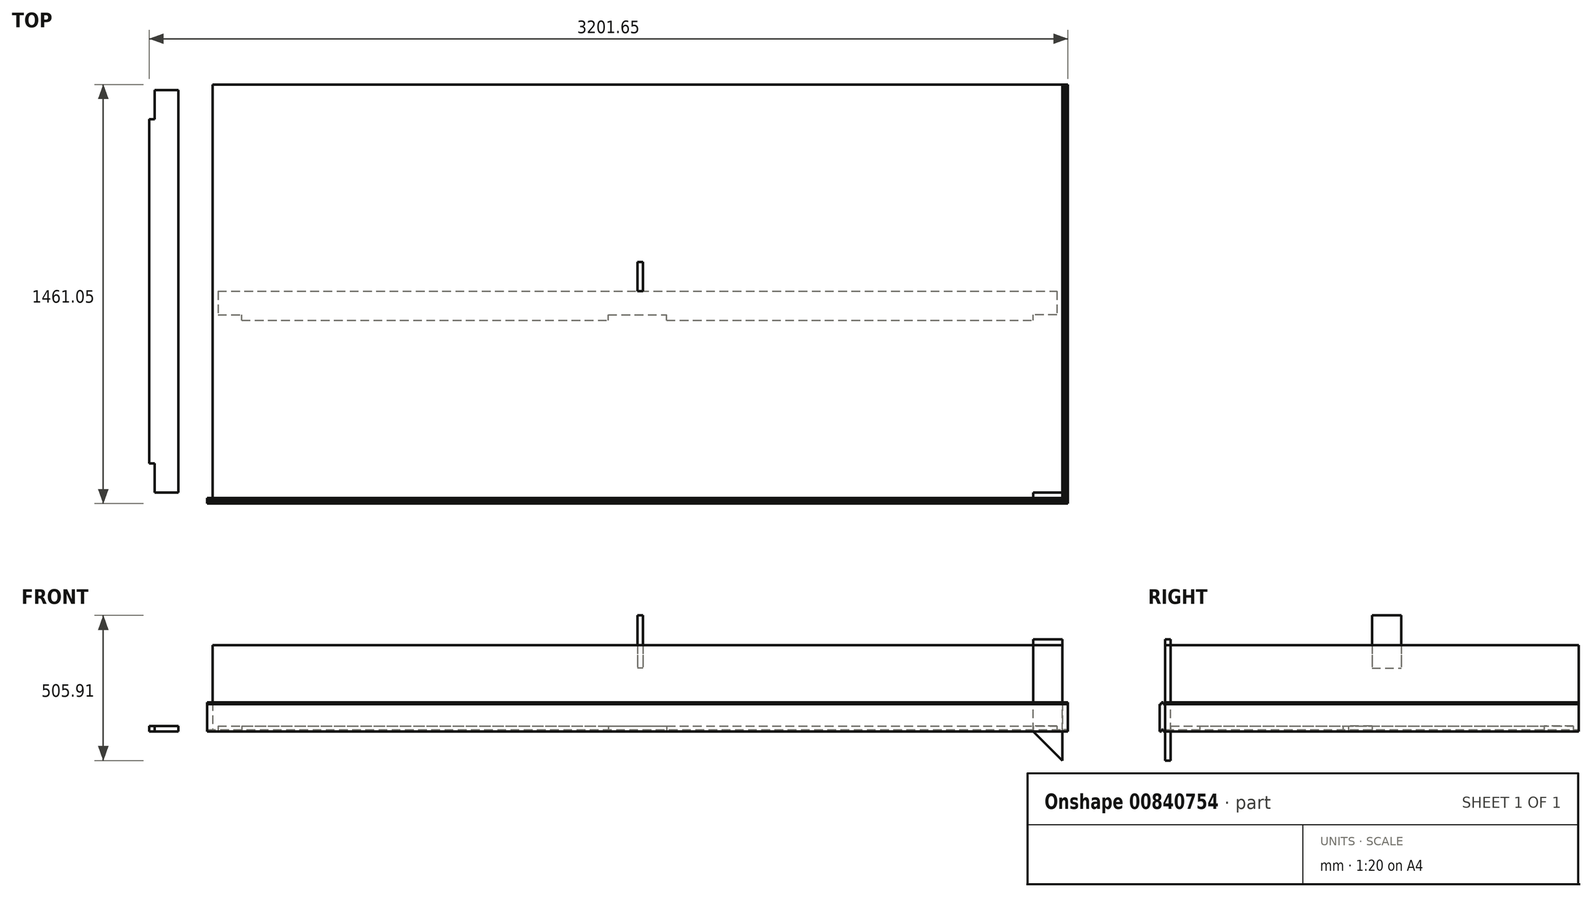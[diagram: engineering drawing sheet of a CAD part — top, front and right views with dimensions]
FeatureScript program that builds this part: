
annotation { "Feature Type Name" : "Feature", "Feature Type Description" : "" }
export const myFeature = defineFeature(function(context is Context, id is Id, definition is map)
    precondition{}
    {
        {
            var Q0;
            Q0=qCreatedBy(makeId("Right.planeOp"),FACE);
            cPlane(context, id + "F0", {"entities" : qUnion([Q0]), "cplaneType" : CPlaneType.OFFSET, "offset" : 1481 * mm, "width" : 150 * mm, "height" : 150 * mm});
        }
        {
            var Q0;
            Q0=qCreatedBy(makeId("Front.planeOp"),FACE);
            cPlane(context, id + "F1", {"entities" : qUnion([Q0]), "cplaneType" : CPlaneType.OFFSET, "offset" : 721 * mm, "width" : 150 * mm, "height" : 150 * mm});
        }
        {
            var Q0;
            Q0=qCreatedBy(makeId("Top.planeOp"),FACE);
            var sketch = newSketch(context, id + "F2", { "sketchPlane" : qUnion([Q0])});
            skLineSegment(sketch, "E0.bottom", {"start": v(1481, 721) * mm, "end": v(-1481, 721) * mm});
            skLineSegment(sketch, "E0.top", {"start": v(1481, -721) * mm, "end": v(-1481, -721) * mm});
            skLineSegment(sketch, "E0.left", {"start": v(1481, 721) * mm, "end": v(1481, -721) * mm});
            skLineSegment(sketch, "E0.right", {"start": v(-1481, 721) * mm, "end": v(-1481, -721) * mm});
            skPoint(sketch, "E0.middle", {"position": v(0, 0) * mm});
            skSolve(sketch);
        }
        {
            var Q0;
            Q0=qSketchRegion(id+"F2",true);
            extrude(context, id + "F3", {"entities" : qUnion([Q0]), "depth" : 300 * mm});
        }
        {
            var Q0;
            Q0=qCreatedBy(id+"F0.planeOp",FACE);
            var sketch = newSketch(context, id + "F4", { "sketchPlane" : qUnion([Q0])});
            skLineSegment(sketch, "E1.bottom", {"start": v(-721, 0) * mm, "end": v(721, 0) * mm});
            skLineSegment(sketch, "E1.top", {"start": v(-721, 101.6) * mm, "end": v(721, 101.6) * mm});
            skLineSegment(sketch, "E1.left", {"start": v(-721, 0) * mm, "end": v(-721, 101.6) * mm});
            skLineSegment(sketch, "E1.right", {"start": v(721, 0) * mm, "end": v(721, 101.6) * mm});
            skPoint(sketch, "E2", {"position": v(0, 0) * mm});
            skSolve(sketch);
        }
        {
            var Q0;
            Q0=qSketchRegion(id+"F4",true);
            extrude(context, id + "F5", {"entities" : qUnion([Q0]), "offsetDistance" : 25 * mm, "depth" : 19.05 * mm});
        }
        {
            var Q0;
            Q0=qCreatedBy(id+"F1.planeOp",FACE);
            var sketch = newSketch(context, id + "F6", { "sketchPlane" : qUnion([Q0])});
            skLineSegment(sketch, "E3.bottom", {"start": v(-1500, 101.6) * mm, "end": v(1500, 101.6) * mm});
            skLineSegment(sketch, "E3.top", {"start": v(-1500, 0) * mm, "end": v(1500, 0) * mm});
            skLineSegment(sketch, "E3.left", {"start": v(-1500, 101.6) * mm, "end": v(-1500, 0) * mm});
            skLineSegment(sketch, "E3.right", {"start": v(1500, 101.6) * mm, "end": v(1500, 0) * mm});
            skPoint(sketch, "E4", {"position": v(0, 0) * mm});
            skSolve(sketch);
        }
        {
            var Q0;
            Q0=qSketchRegion(id+"F6",true);
            extrude(context, id + "F7", {"entities" : qUnion([Q0]), "offsetDistance" : 25 * mm, "depth" : 19.05 * mm});
        }
        {
            var Q0;
            Q0=makeQuery(id+"F3.opExtrude","CAP_FACE",FACE,{"disambiguationData":[OSD([sQuery(id+"F2.wireOp",EDGE,"E0.bottom"),sQuery(id+"F2.wireOp",EDGE,"E0.top"),sQuery(id+"F2.wireOp",EDGE,"E0.left"),sQuery(id+"F2.wireOp",EDGE,"E0.right")])],"isStart":false});
            var sketch = newSketch(context, id + "F8", { "sketchPlane" : qUnion([Q0])});
            skFitSpline(sketch, "E5", {"points": [v(-9.76, -247.93) * mm, v(-14.36, -247) * mm, v(-98.7, -232.48) * mm, v(-197.18, -215.67) * mm]});
            skFitSpline(sketch, "E6", {"points": [v(-197.18, -215.67) * mm, v(-303.5, -197.52) * mm, v(-377.79, -184.02) * mm, v(-380.05, -182.43) * mm]});
            skFitSpline(sketch, "E7", {"points": [v(-380.05, -182.43) * mm, v(-386.35, -178.01) * mm, v(-389.22, -172.54) * mm, v(-390.38, -162.7) * mm]});
            skLineSegment(sketch, "E8", {"start": v(-390.38, -162.7) * mm, "end": v(-391.49, -153.38) * mm});
            skLineSegment(sketch, "E9", {"start": v(-391.49, -153.38) * mm, "end": v(-463.29, -153.35) * mm});
            skFitSpline(sketch, "E10", {"points": [v(-463.29, -153.35) * mm, v(-540.74, -153.32) * mm, v(-542.21, -153.15) * mm, v(-546.84, -143.5) * mm]});
            skFitSpline(sketch, "E11", {"points": [v(-546.84, -143.5) * mm, v(-550.32, -136.23) * mm, v(-547.5, -129.03) * mm, v(-539.62, -125.02) * mm]});
            skFitSpline(sketch, "E12", {"points": [v(-539.62, -125.02) * mm, v(-533.58, -121.95) * mm, v(-503.94, -121.77) * mm, v(0.65, -121.77) * mm]});
            skFitSpline(sketch, "E13", {"points": [v(0.65, -121.77) * mm, v(385.66, -121.76) * mm, v(536.18, -122.34) * mm, v(540.43, -123.82) * mm]});
            skFitSpline(sketch, "E14", {"points": [v(540.43, -123.82) * mm, v(543.67, -124.95) * mm, v(547.14, -127.4) * mm, v(548.14, -129.27) * mm]});
            skFitSpline(sketch, "E15", {"points": [v(548.14, -129.27) * mm, v(551.05, -134.7) * mm, v(550.26, -143.3) * mm, v(546.41, -148.06) * mm]});
            skLineSegment(sketch, "E16", {"start": v(546.41, -148.06) * mm, "end": v(542.86, -152.45) * mm});
            skLineSegment(sketch, "E17", {"start": v(542.86, -152.45) * mm, "end": v(467.85, -153.38) * mm});
            skLineSegment(sketch, "E18", {"start": v(467.85, -153.38) * mm, "end": v(392.83, -154.3) * mm});
            skLineSegment(sketch, "E19", {"start": v(392.83, -154.3) * mm, "end": v(392.5, -162.05) * mm});
            skFitSpline(sketch, "E20", {"points": [v(392.5, -162.05) * mm, v(391.99, -173.78) * mm, v(387.68, -180.46) * mm, v(378.46, -183.85) * mm]});
            skFitSpline(sketch, "E21", {"points": [v(378.46, -183.85) * mm, v(371.97, -186.24) * mm, v(2.57, -250.58) * mm, v(-0.47, -249.85) * mm]});
            skFitSpline(sketch, "E22", {"points": [v(-0.47, -249.85) * mm, v(-0.98, -249.73) * mm, v(-5.16, -248.87) * mm, v(-9.76, -247.93) * mm]});
            skLineSegment(sketch, "E23", {"start": v(-9.76, -247.93) * mm, "end": v(-9.76, -247.93) * mm});
            skFitSpline(sketch, "E24", {"points": [v(163.18, -91.34) * mm, v(144.56, -86.99) * mm, v(127.82, -80.58) * mm, v(118.25, -74.15) * mm]});
            skLineSegment(sketch, "E25", {"start": v(118.25, -74.15) * mm, "end": v(108.82, -67.8) * mm});
            skLineSegment(sketch, "E26", {"start": v(108.82, -67.8) * mm, "end": v(101.7, -74.22) * mm});
            skFitSpline(sketch, "E27", {"points": [v(101.7, -74.22) * mm, v(92.92, -82.15) * mm, v(86.06, -85.78) * mm, v(75.22, -88.2) * mm]});
            skFitSpline(sketch, "E28", {"points": [v(75.22, -88.2) * mm, v(52.86, -93.22) * mm, v(44.33, -75.76) * mm, v(50.52, -37.64) * mm]});
            skFitSpline(sketch, "E29", {"points": [v(50.52, -37.64) * mm, v(54.63, -12.34) * mm, v(54.44, -8.7) * mm, v(48.9, -6.17) * mm]});
            skFitSpline(sketch, "E30", {"points": [v(48.9, -6.17) * mm, v(42.7, -3.35) * mm, v(36.64, -7.44) * mm, v(29.87, -18.99) * mm]});
            skFitSpline(sketch, "E31", {"points": [v(29.87, -18.99) * mm, v(21.01, -34.1) * mm, v(18.43, -44.15) * mm, v(20.53, -55.3) * mm]});
            skFitSpline(sketch, "E32", {"points": [v(20.53, -55.3) * mm, v(21.54, -60.66) * mm, v(22.46, -68.35) * mm, v(22.57, -72.38) * mm]});
            skFitSpline(sketch, "E33", {"points": [v(22.57, -72.38) * mm, v(22.76, -78.97) * mm, v(22, -80.26) * mm, v(14.95, -85.23) * mm]});
            skFitSpline(sketch, "E34", {"points": [v(14.95, -85.23) * mm, v(4.39, -92.68) * mm, v(-7.54, -93.24) * mm, v(-11.04, -86.43) * mm]});
            skFitSpline(sketch, "E35", {"points": [v(-11.04, -86.43) * mm, v(-13.95, -80.76) * mm, v(-14.16, -56.28) * mm, v(-11.54, -26.93) * mm]});
            skFitSpline(sketch, "E36", {"points": [v(-11.54, -26.93) * mm, v(-9.2, -0.66) * mm, v(-9.84, 2.83) * mm, v(-17.07, 2.83) * mm]});
            skFitSpline(sketch, "E37", {"points": [v(-17.07, 2.83) * mm, v(-23.9, 2.83) * mm, v(-30.46, -4.7) * mm, v(-38.87, -22.23) * mm]});
            skFitSpline(sketch, "E38", {"points": [v(-38.87, -22.23) * mm, v(-45.93, -36.93) * mm, v(-46.62, -45.33) * mm, v(-42.27, -63.77) * mm]});
            skFitSpline(sketch, "E39", {"points": [v(-42.27, -63.77) * mm, v(-38.91, -78.01) * mm, v(-39.9, -80.3) * mm, v(-52.19, -87) * mm]});
            skFitSpline(sketch, "E40", {"points": [v(-52.19, -87) * mm, v(-68.26, -95.75) * mm, v(-75.2, -92.86) * mm, v(-77.56, -76.43) * mm]});
            skLineSegment(sketch, "E41", {"start": v(-77.56, -76.43) * mm, "end": v(-78.86, -67.36) * mm});
            skLineSegment(sketch, "E42", {"start": v(-78.86, -67.36) * mm, "end": v(-86.62, -74.83) * mm});
            skFitSpline(sketch, "E43", {"points": [v(-86.62, -74.83) * mm, v(-97.05, -84.9) * mm, v(-104.92, -88.54) * mm, v(-116.78, -88.82) * mm]});
            skFitSpline(sketch, "E44", {"points": [v(-116.78, -88.82) * mm, v(-128.34, -89.1) * mm, v(-132.94, -86) * mm, v(-138.3, -74.35) * mm]});
            skFitSpline(sketch, "E45", {"points": [v(-138.3, -74.35) * mm, v(-144.12, -61.65) * mm, v(-141.58, -31.54) * mm, v(-133.32, -15.58) * mm]});
            skLineSegment(sketch, "E46", {"start": v(-133.32, -15.58) * mm, "end": v(-130.44, -10) * mm});
            skLineSegment(sketch, "E47", {"start": v(-130.44, -10) * mm, "end": v(-141.2, -10.56) * mm});
            skLineSegment(sketch, "E48", {"start": v(-141.2, -10.56) * mm, "end": v(-151.94, -11.12) * mm});
            skLineSegment(sketch, "E49", {"start": v(-151.94, -11.12) * mm, "end": v(-155.34, -25.07) * mm});
            skFitSpline(sketch, "E50", {"points": [v(-155.34, -25.07) * mm, v(-157.97, -35.9) * mm, v(-158.52, -43.56) * mm, v(-157.8, -59.34) * mm]});
            skFitSpline(sketch, "E51", {"points": [v(-157.8, -59.34) * mm, v(-157.29, -70.85) * mm, v(-157.67, -81.12) * mm, v(-158.7, -83.03) * mm]});
            skFitSpline(sketch, "E52", {"points": [v(-158.7, -83.03) * mm, v(-161.25, -87.81) * mm, v(-170.24, -92.01) * mm, v(-177.92, -92.01) * mm]});
            skFitSpline(sketch, "E53", {"points": [v(-177.92, -92.01) * mm, v(-186.08, -92.01) * mm, v(-189.42, -87.45) * mm, v(-191.2, -73.87) * mm]});
            skLineSegment(sketch, "E54", {"start": v(-191.2, -73.87) * mm, "end": v(-192.48, -64.09) * mm});
            skLineSegment(sketch, "E55", {"start": v(-192.48, -64.09) * mm, "end": v(-200.42, -71.4) * mm});
            skFitSpline(sketch, "E56", {"points": [v(-200.42, -71.4) * mm, v(-209.89, -80.13) * mm, v(-220.17, -85.65) * mm, v(-231.87, -88.27) * mm]});
            skFitSpline(sketch, "E57", {"points": [v(-231.87, -88.27) * mm, v(-243.7, -90.92) * mm, v(-250.08, -87.49) * mm, v(-254.4, -76.16) * mm]});
            skLineSegment(sketch, "E58", {"start": v(-254.4, -76.16) * mm, "end": v(-257.65, -67.68) * mm});
            skLineSegment(sketch, "E59", {"start": v(-257.65, -67.68) * mm, "end": v(-262.94, -74.1) * mm});
            skFitSpline(sketch, "E60", {"points": [v(-262.94, -74.1) * mm, v(-279.38, -94.04) * mm, v(-316.37, -95.84) * mm, v(-331.85, -77.45) * mm]});
            skFitSpline(sketch, "E61", {"points": [v(-331.85, -77.45) * mm, v(-339.17, -68.75) * mm, v(-341.42, -59.86) * mm, v(-340.14, -44.75) * mm]});
            skFitSpline(sketch, "E62", {"points": [v(-340.14, -44.75) * mm, v(-338.13, -20.94) * mm, v(-329.14, -1.86) * mm, v(-313.1, 12.61) * mm]});
            skFitSpline(sketch, "E63", {"points": [v(-313.1, 12.61) * mm, v(-297.94, 26.32) * mm, v(-276.95, 32.69) * mm, v(-259.7, 28.82) * mm]});
            skFitSpline(sketch, "E64", {"points": [v(-259.7, 28.82) * mm, v(-252.55, 27.22) * mm, v(-250.45, 27.38) * mm, v(-247.85, 29.73) * mm]});
            skFitSpline(sketch, "E65", {"points": [v(-247.85, 29.73) * mm, v(-240.93, 36) * mm, v(-226.99, 30.32) * mm, v(-220.73, 18.7) * mm]});
            skLineSegment(sketch, "E66", {"start": v(-220.73, 18.7) * mm, "end": v(-217.21, 12.17) * mm});
            skLineSegment(sketch, "E67", {"start": v(-217.21, 12.17) * mm, "end": v(-223.2, 0.02) * mm});
            skFitSpline(sketch, "E68", {"points": [v(-223.2, 0.02) * mm, v(-228.92, -11.58) * mm, v(-229.19, -13.1) * mm, v(-229.16, -33.94) * mm]});
            skFitSpline(sketch, "E69", {"points": [v(-229.16, -33.94) * mm, v(-229.13, -57.9) * mm, v(-228.1, -61.48) * mm, v(-221.81, -59.49) * mm]});
            skFitSpline(sketch, "E70", {"points": [v(-221.81, -59.49) * mm, v(-215.07, -57.35) * mm, v(-188.28, -30.28) * mm, v(-188.28, -25.6) * mm]});
            skFitSpline(sketch, "E71", {"points": [v(-188.28, -25.6) * mm, v(-188.28, -23.36) * mm, v(-186.22, -15.85) * mm, v(-183.7, -8.92) * mm]});
            skFitSpline(sketch, "E72", {"points": [v(-183.7, -8.92) * mm, v(-179.26, 3.33) * mm, v(-179.23, 3.78) * mm, v(-182.54, 7.44) * mm]});
            skFitSpline(sketch, "E73", {"points": [v(-182.54, 7.44) * mm, v(-188.48, 13.98) * mm, v(-190.53, 19.67) * mm, v(-189.3, 26.21) * mm]});
            skFitSpline(sketch, "E74", {"points": [v(-189.3, 26.21) * mm, v(-187.82, 34.15) * mm, v(-182.12, 38.16) * mm, v(-172.31, 38.16) * mm]});
            skFitSpline(sketch, "E75", {"points": [v(-172.31, 38.16) * mm, v(-163.16, 38.16) * mm, v(-156.23, 32.34) * mm, v(-150.73, 20.03) * mm]});
            skFitSpline(sketch, "E76", {"points": [v(-150.73, 20.03) * mm, v(-147.7, 13.24) * mm, v(-146.4, 12.12) * mm, v(-141.55, 12.12) * mm]});
            skFitSpline(sketch, "E77", {"points": [v(-141.55, 12.12) * mm, v(-138.45, 12.12) * mm, v(-130.4, 14.33) * mm, v(-123.66, 17.03) * mm]});
            skFitSpline(sketch, "E78", {"points": [v(-123.66, 17.03) * mm, v(-109.3, 22.78) * mm, v(-107.41, 22.17) * mm, v(-101.2, 9.8) * mm]});
            skLineSegment(sketch, "E79", {"start": v(-101.2, 9.8) * mm, "end": v(-96.87, 1.18) * mm});
            skLineSegment(sketch, "E80", {"start": v(-96.87, 1.18) * mm, "end": v(-104.6, -26.95) * mm});
            skFitSpline(sketch, "E81", {"points": [v(-104.6, -26.95) * mm, v(-115.26, -65.72) * mm, v(-113.52, -68.38) * mm, v(-91.12, -47.46) * mm]});
            skLineSegment(sketch, "E82", {"start": v(-91.12, -47.46) * mm, "end": v(-77.26, -34.51) * mm});
            skLineSegment(sketch, "E83", {"start": v(-77.26, -34.51) * mm, "end": v(-76.15, -22.7) * mm});
            skFitSpline(sketch, "E84", {"points": [v(-76.15, -22.7) * mm, v(-74.76, -7.77) * mm, v(-68.68, 10.87) * mm, v(-61.04, 23.61) * mm]});
            skFitSpline(sketch, "E85", {"points": [v(-61.04, 23.61) * mm, v(-56.21, 31.68) * mm, v(-54.07, 33.61) * mm, v(-49.45, 34.07) * mm]});
            skFitSpline(sketch, "E86", {"points": [v(-49.45, 34.07) * mm, v(-44.95, 34.52) * mm, v(-42.63, 33.32) * mm, v(-38.15, 28.2) * mm]});
            skFitSpline(sketch, "E87", {"points": [v(-38.15, 28.2) * mm, v(-35.04, 24.67) * mm, v(-32.16, 20.74) * mm, v(-31.73, 19.46) * mm]});
            skFitSpline(sketch, "E88", {"points": [v(-31.73, 19.46) * mm, v(-31.21, 17.9) * mm, v(-28.37, 19.02) * mm, v(-23, 22.9) * mm]});
            skFitSpline(sketch, "E89", {"points": [v(-23, 22.9) * mm, v(-11.96, 30.9) * mm, v(-1.17, 32.3) * mm, v(9.54, 27.1) * mm]});
            skFitSpline(sketch, "E90", {"points": [v(9.54, 27.1) * mm, v(18.23, 22.9) * mm, v(22.7, 17.7) * mm, v(24.79, 9.4) * mm]});
            skLineSegment(sketch, "E91", {"start": v(24.79, 9.4) * mm, "end": v(26.04, 4.44) * mm});
            skLineSegment(sketch, "E92", {"start": v(26.04, 4.44) * mm, "end": v(30.92, 9.1) * mm});
            skFitSpline(sketch, "E93", {"points": [v(30.92, 9.1) * mm, v(43.6, 21.22) * mm, v(66.06, 25.1) * mm, v(77.8, 17.18) * mm]});
            skFitSpline(sketch, "E94", {"points": [v(77.8, 17.18) * mm, v(81.26, 14.85) * mm, v(85.14, 10.88) * mm, v(86.42, 8.35) * mm]});
            skFitSpline(sketch, "E95", {"points": [v(86.42, 8.35) * mm, v(90.04, 1.18) * mm, v(89.21, -14.95) * mm, v(84.14, -35.88) * mm]});
            skFitSpline(sketch, "E96", {"points": [v(84.14, -35.88) * mm, v(81.59, -46.43) * mm, v(79.5, -56.26) * mm, v(79.5, -57.73) * mm]});
            skFitSpline(sketch, "E97", {"points": [v(79.5, -57.73) * mm, v(79.5, -63.6) * mm, v(86.26, -59.69) * mm, v(100.97, -45.33) * mm]});
            skFitSpline(sketch, "E98", {"points": [v(100.97, -45.33) * mm, v(110.63, -35.9) * mm, v(117.25, -30.77) * mm, v(118.65, -31.64) * mm]});
            skFitSpline(sketch, "E99", {"points": [v(118.65, -31.64) * mm, v(120.17, -32.58) * mm, v(120.56, -36.5) * mm, v(119.89, -43.92) * mm]});
            skFitSpline(sketch, "E100", {"points": [v(119.89, -43.92) * mm, v(118.95, -54.29) * mm, v(119.1, -54.82) * mm, v(123.1, -54.82) * mm]});
            skFitSpline(sketch, "E101", {"points": [v(123.1, -54.82) * mm, v(127.02, -54.82) * mm, v(127.36, -53.84) * mm, v(128.4, -39.48) * mm]});
            skFitSpline(sketch, "E102", {"points": [v(128.4, -39.48) * mm, v(130.72, -7.09) * mm, v(148.03, 43.77) * mm, v(160.6, 55.09) * mm]});
            skFitSpline(sketch, "E103", {"points": [v(160.6, 55.09) * mm, v(178.01, 70.78) * mm, v(179.9, 58.14) * mm, v(168.42, 2.83) * mm]});
            skFitSpline(sketch, "E104", {"points": [v(168.42, 2.83) * mm, v(163.73, -19.8) * mm, v(158.67, -63.5) * mm, v(160.5, -65.68) * mm]});
            skFitSpline(sketch, "E105", {"points": [v(160.5, -65.68) * mm, v(161.76, -67.18) * mm, v(175.96, -69.61) * mm, v(183.63, -69.64) * mm]});
            skFitSpline(sketch, "E106", {"points": [v(183.63, -69.64) * mm, v(200.98, -69.71) * mm, v(215.69, -61.64) * mm, v(220.83, -49.22) * mm]});
            skFitSpline(sketch, "E107", {"points": [v(220.83, -49.22) * mm, v(224.51, -40.34) * mm, v(222.43, -16.02) * mm, v(217.28, -7.68) * mm]});
            skFitSpline(sketch, "E108", {"points": [v(217.28, -7.68) * mm, v(213.13, -0.96) * mm, v(212.95, -0.9) * mm, v(200.63, -0.9) * mm]});
            skFitSpline(sketch, "E109", {"points": [v(200.63, -0.9) * mm, v(187.27, -0.9) * mm, v(181.1, 1.8) * mm, v(179.39, 8.35) * mm]});
            skFitSpline(sketch, "E110", {"points": [v(179.39, 8.35) * mm, v(178.82, 10.5) * mm, v(179.82, 13.89) * mm, v(181.7, 16.2) * mm]});
            skFitSpline(sketch, "E111", {"points": [v(181.7, 16.2) * mm, v(184.4, 19.56) * mm, v(187.56, 20.46) * mm, v(199.63, 21.31) * mm]});
            skFitSpline(sketch, "E112", {"points": [v(199.63, 21.31) * mm, v(213.63, 22.3) * mm, v(214.4, 22.6) * mm, v(217.02, 27.93) * mm]});
            skFitSpline(sketch, "E113", {"points": [v(217.02, 27.93) * mm, v(218.53, 31) * mm, v(219.77, 38.53) * mm, v(219.78, 44.67) * mm]});
            skFitSpline(sketch, "E114", {"points": [v(219.78, 44.67) * mm, v(219.8, 64.17) * mm, v(211.17, 71.67) * mm, v(187.07, 73.1) * mm]});
            skFitSpline(sketch, "E115", {"points": [v(187.07, 73.1) * mm, v(170.05, 74.11) * mm, v(157.7, 71.45) * mm, v(139.99, 62.97) * mm]});
            skFitSpline(sketch, "E116", {"points": [v(139.99, 62.97) * mm, v(124.82, 55.7) * mm, v(118.55, 54.98) * mm, v(118.55, 60.51) * mm]});
            skFitSpline(sketch, "E117", {"points": [v(118.55, 60.51) * mm, v(118.55, 70.5) * mm, v(143.11, 88.38) * mm, v(165.9, 94.95) * mm]});
            skFitSpline(sketch, "E118", {"points": [v(165.9, 94.95) * mm, v(181.16, 99.36) * mm, v(211.58, 97.92) * mm, v(227.33, 92.04) * mm]});
            skFitSpline(sketch, "E119", {"points": [v(227.33, 92.04) * mm, v(241.91, 86.6) * mm, v(254.67, 73.92) * mm, v(257.71, 61.83) * mm]});
            skFitSpline(sketch, "E120", {"points": [v(257.71, 61.83) * mm, v(262.48, 42.9) * mm, v(259.33, 31.38) * mm, v(245.79, 18.17) * mm]});
            skFitSpline(sketch, "E121", {"points": [v(245.79, 18.17) * mm, v(240.28, 12.8) * mm, v(236.48, 8.4) * mm, v(237.34, 8.4) * mm]});
            skFitSpline(sketch, "E122", {"points": [v(237.34, 8.4) * mm, v(241.01, 8.4) * mm, v(256.17, -7.19) * mm, v(259.81, -14.71) * mm]});
            skFitSpline(sketch, "E123", {"points": [v(259.81, -14.71) * mm, v(265.46, -26.39) * mm, v(265.68, -49.04) * mm, v(260.25, -59.68) * mm]});
            skFitSpline(sketch, "E124", {"points": [v(260.25, -59.68) * mm, v(254.38, -71.16) * mm, v(239.5, -83.55) * mm, v(225.92, -88.28) * mm]});
            skFitSpline(sketch, "E125", {"points": [v(225.92, -88.28) * mm, v(211.44, -93.33) * mm, v(178.53, -94.93) * mm, v(163.18, -91.34) * mm]});
            skFitSpline(sketch, "E126", {"points": [v(-281.84, -62.14) * mm, v(-267.85, -56.85) * mm, v(-259.05, -41.8) * mm, v(-258.98, -23.08) * mm]});
            skFitSpline(sketch, "E127", {"points": [v(-258.98, -23.08) * mm, v(-258.96, -16.37) * mm, v(-258.05, -6.04) * mm, v(-256.95, -0.12) * mm]});
            skFitSpline(sketch, "E128", {"points": [v(-256.95, -0.12) * mm, v(-255.86, 5.8) * mm, v(-255.42, 11.09) * mm, v(-255.98, 11.64) * mm]});
            skFitSpline(sketch, "E129", {"points": [v(-255.98, 11.64) * mm, v(-257.93, 13.6) * mm, v(-273.99, 6.15) * mm, v(-282.7, -0.75) * mm]});
            skFitSpline(sketch, "E130", {"points": [v(-282.7, -0.75) * mm, v(-295.24, -10.66) * mm, v(-302.1, -24.16) * mm, v(-303.18, -41.06) * mm]});
            skFitSpline(sketch, "E131", {"points": [v(-303.18, -41.06) * mm, v(-303.98, -53.62) * mm, v(-303.72, -54.84) * mm, v(-299.24, -59.32) * mm]});
            skFitSpline(sketch, "E132", {"points": [v(-299.24, -59.32) * mm, v(-294.03, -64.53) * mm, v(-289.93, -65.2) * mm, v(-281.84, -62.14) * mm]});
            skFitSpline(sketch, "E133", {"points": [v(-459.3, -89.94) * mm, v(-464.48, -84.62) * mm, v(-460.7, -35.47) * mm, v(-453.32, -12.23) * mm]});
            skFitSpline(sketch, "E134", {"points": [v(-453.32, -12.23) * mm, v(-452.15, -8.52) * mm, v(-452.73, -8.33) * mm, v(-465.23, -8.33) * mm]});
            skFitSpline(sketch, "E135", {"points": [v(-465.23, -8.33) * mm, v(-476.68, -8.33) * mm, v(-478.37, -7.9) * mm, v(-478.37, -4.96) * mm]});
            skFitSpline(sketch, "E136", {"points": [v(-478.37, -4.96) * mm, v(-478.37, 0.26) * mm, v(-468.99, 8.03) * mm, v(-457.1, 12.63) * mm]});
            skLineSegment(sketch, "E137", {"start": v(-457.1, 12.63) * mm, "end": v(-446.32, 16.8) * mm});
            skLineSegment(sketch, "E138", {"start": v(-446.32, 16.8) * mm, "end": v(-438.43, 39.1) * mm});
            skFitSpline(sketch, "E139", {"points": [v(-438.43, 39.1) * mm, v(-434.08, 51.37) * mm, v(-429.87, 62.96) * mm, v(-429.07, 64.87) * mm]});
            skFitSpline(sketch, "E140", {"points": [v(-429.07, 64.87) * mm, v(-427.72, 68.05) * mm, v(-428.28, 68.22) * mm, v(-435.78, 67) * mm]});
            skFitSpline(sketch, "E141", {"points": [v(-435.78, 67) * mm, v(-447.95, 65.04) * mm, v(-458.5, 59.86) * mm, v(-467.75, 51.34) * mm]});
            skFitSpline(sketch, "E142", {"points": [v(-467.75, 51.34) * mm, v(-479.66, 40.36) * mm, v(-483.95, 41.51) * mm, v(-483.95, 55.7) * mm]});
            skFitSpline(sketch, "E143", {"points": [v(-483.95, 55.7) * mm, v(-483.95, 68.83) * mm, v(-467.73, 83.32) * mm, v(-445.28, 90.26) * mm]});
            skFitSpline(sketch, "E144", {"points": [v(-445.28, 90.26) * mm, v(-427.1, 95.87) * mm, v(-406.05, 97.33) * mm, v(-358.74, 96.25) * mm]});
            skFitSpline(sketch, "E145", {"points": [v(-358.74, 96.25) * mm, v(-311.18, 95.17) * mm, v(-311.95, 95.43) * mm, v(-317.58, 82.22) * mm]});
            skFitSpline(sketch, "E146", {"points": [v(-317.58, 82.22) * mm, v(-323.64, 68.03) * mm, v(-324, 67.91) * mm, v(-360.96, 67.88) * mm]});
            skLineSegment(sketch, "E147", {"start": v(-360.96, 67.88) * mm, "end": v(-393.76, 67.85) * mm});
            skLineSegment(sketch, "E148", {"start": v(-393.76, 67.85) * mm, "end": v(-398.66, 47.9) * mm});
            skFitSpline(sketch, "E149", {"points": [v(-398.66, 47.9) * mm, v(-401.36, 36.91) * mm, v(-403.87, 26.67) * mm, v(-404.24, 25.14) * mm]});
            skFitSpline(sketch, "E150", {"points": [v(-404.24, 25.14) * mm, v(-404.8, 22.8) * mm, v(-401.23, 22.27) * mm, v(-381.74, 21.83) * mm]});
            skFitSpline(sketch, "E151", {"points": [v(-381.74, 21.83) * mm, v(-367.15, 21.5) * mm, v(-358.1, 20.53) * mm, v(-357.28, 19.21) * mm]});
            skFitSpline(sketch, "E152", {"points": [v(-357.28, 19.21) * mm, v(-355.76, 16.75) * mm, v(-359.89, 2.02) * mm, v(-363.24, -2.01) * mm]});
            skFitSpline(sketch, "E153", {"points": [v(-363.24, -2.01) * mm, v(-365.2, -4.38) * mm, v(-369.3, -4.62) * mm, v(-389.06, -3.54) * mm]});
            skLineSegment(sketch, "E154", {"start": v(-389.06, -3.54) * mm, "end": v(-412.56, -2.27) * mm});
            skLineSegment(sketch, "E155", {"start": v(-412.56, -2.27) * mm, "end": v(-416.52, -18.78) * mm});
            skFitSpline(sketch, "E156", {"points": [v(-416.52, -18.78) * mm, v(-421.04, -37.64) * mm, v(-423.77, -53.93) * mm, v(-425.45, -72.08) * mm]});
            skFitSpline(sketch, "E157", {"points": [v(-425.45, -72.08) * mm, v(-426.44, -82.86) * mm, v(-427.3, -85.14) * mm, v(-431.33, -87.78) * mm]});
            skFitSpline(sketch, "E158", {"points": [v(-431.33, -87.78) * mm, v(-437.41, -91.77) * mm, v(-456.13, -93.2) * mm, v(-459.3, -89.94) * mm]});
            skFitSpline(sketch, "E159", {"points": [v(317.5, -88.5) * mm, v(302.9, -83.79) * mm, v(289.51, -71.3) * mm, v(285.81, -58.96) * mm]});
            skFitSpline(sketch, "E160", {"points": [v(285.81, -58.96) * mm, v(282.17, -46.8) * mm, v(284.25, -22.14) * mm, v(289.96, -9.87) * mm]});
            skFitSpline(sketch, "E161", {"points": [v(289.96, -9.87) * mm, v(299.26, 10.12) * mm, v(316.09, 24.32) * mm, v(335.9, 28.9) * mm]});
            skFitSpline(sketch, "E162", {"points": [v(335.9, 28.9) * mm, v(354.07, 33.1) * mm, v(378.44, 28.13) * mm, v(386.33, 18.63) * mm]});
            skFitSpline(sketch, "E163", {"points": [v(386.33, 18.63) * mm, v(390.02, 14.18) * mm, v(386.8, 12.82) * mm, v(369.86, 11.65) * mm]});
            skFitSpline(sketch, "E164", {"points": [v(369.86, 11.65) * mm, v(362, 11.12) * mm, v(352.6, 9.43) * mm, v(348.96, 7.91) * mm]});
            skFitSpline(sketch, "E165", {"points": [v(348.96, 7.91) * mm, v(331.95, 0.8) * mm, v(320.77, -16.17) * mm, v(320.52, -35.3) * mm]});
            skFitSpline(sketch, "E166", {"points": [v(320.52, -35.3) * mm, v(320.22, -57.93) * mm, v(334.52, -68.41) * mm, v(357.15, -62.13) * mm]});
            skLineSegment(sketch, "E167", {"start": v(357.15, -62.13) * mm, "end": v(364.23, -60.16) * mm});
            skLineSegment(sketch, "E168", {"start": v(364.23, -60.16) * mm, "end": v(357.84, -53.09) * mm});
            skFitSpline(sketch, "E169", {"points": [v(357.84, -53.09) * mm, v(336.45, -29.41) * mm, v(349.03, 6.55) * mm, v(378.7, 6.55) * mm]});
            skFitSpline(sketch, "E170", {"points": [v(378.7, 6.55) * mm, v(389.23, 6.55) * mm, v(395.06, 3.8) * mm, v(399.43, -3.17) * mm]});
            skFitSpline(sketch, "E171", {"points": [v(399.43, -3.17) * mm, v(402.65, -8.3) * mm, v(403.12, -11.47) * mm, v(402.44, -23.2) * mm]});
            skFitSpline(sketch, "E172", {"points": [v(402.44, -23.2) * mm, v(402, -30.88) * mm, v(401.02, -39.04) * mm, v(400.27, -41.34) * mm]});
            skFitSpline(sketch, "E173", {"points": [v(400.27, -41.34) * mm, v(398.58, -46.51) * mm, v(402.33, -46.92) * mm, v(411.06, -42.52) * mm]});
            skFitSpline(sketch, "E174", {"points": [v(411.06, -42.52) * mm, v(421.31, -37.33) * mm, v(425.37, -32.45) * mm, v(425.44, -25.2) * mm]});
            skFitSpline(sketch, "E175", {"points": [v(425.44, -25.2) * mm, v(425.48, -21.55) * mm, v(426.6, -12.92) * mm, v(427.94, -6.02) * mm]});
            skFitSpline(sketch, "E176", {"points": [v(427.94, -6.02) * mm, v(429.27, 0.87) * mm, v(429.94, 6.94) * mm, v(429.42, 7.46) * mm]});
            skFitSpline(sketch, "E177", {"points": [v(429.42, 7.46) * mm, v(428.9, 7.98) * mm, v(425.6, 8.4) * mm, v(422.07, 8.4) * mm]});
            skFitSpline(sketch, "E178", {"points": [v(422.07, 8.4) * mm, v(415.71, 8.4) * mm, v(415.67, 8.46) * mm, v(416.93, 15.14) * mm]});
            skFitSpline(sketch, "E179", {"points": [v(416.93, 15.14) * mm, v(418.93, 25.81) * mm, v(421.68, 28.86) * mm, v(429.3, 28.86) * mm]});
            skFitSpline(sketch, "E180", {"points": [v(429.3, 28.86) * mm, v(435.8, 28.86) * mm, v(436.17, 29.23) * mm, v(439.97, 39.55) * mm]});
            skFitSpline(sketch, "E181", {"points": [v(439.97, 39.55) * mm, v(450.84, 69.05) * mm, v(465.01, 75.94) * mm, v(473.83, 56) * mm]});
            skLineSegment(sketch, "E182", {"start": v(473.83, 56) * mm, "end": v(477.45, 47.84) * mm});
            skLineSegment(sketch, "E183", {"start": v(477.45, 47.84) * mm, "end": v(472.82, 39.75) * mm});
            skFitSpline(sketch, "E184", {"points": [v(472.82, 39.75) * mm, v(470.27, 35.3) * mm, v(468.18, 31.02) * mm, v(468.17, 30.25) * mm]});
            skFitSpline(sketch, "E185", {"points": [v(468.17, 30.25) * mm, v(468.15, 29.49) * mm, v(474, 28.86) * mm, v(481.16, 28.86) * mm]});
            skFitSpline(sketch, "E186", {"points": [v(481.16, 28.86) * mm, v(493.59, 28.86) * mm, v(494.18, 28.66) * mm, v(494.18, 24.49) * mm]});
            skFitSpline(sketch, "E187", {"points": [v(494.18, 24.49) * mm, v(494.18, 22.08) * mm, v(493.26, 17.48) * mm, v(492.14, 14.26) * mm]});
            skFitSpline(sketch, "E188", {"points": [v(492.14, 14.26) * mm, v(490.1, 8.41) * mm, v(490.07, 8.4) * mm, v(476.53, 8.4) * mm]});
            skFitSpline(sketch, "E189", {"points": [v(476.53, 8.4) * mm, v(466.58, 8.4) * mm, v(462.7, 7.7) * mm, v(461.96, 5.79) * mm]});
            skFitSpline(sketch, "E190", {"points": [v(461.96, 5.79) * mm, v(461.4, 4.35) * mm, v(459.93, -6.74) * mm, v(458.69, -18.85) * mm]});
            skFitSpline(sketch, "E191", {"points": [v(458.69, -18.85) * mm, v(456.19, -43.13) * mm, v(457.42, -58.1) * mm, v(462.05, -59.89) * mm]});
            skFitSpline(sketch, "E192", {"points": [v(462.05, -59.89) * mm, v(466.54, -61.6) * mm, v(480.7, -53.25) * mm, v(493.44, -41.34) * mm]});
            skFitSpline(sketch, "E193", {"points": [v(493.44, -41.34) * mm, v(499.73, -35.46) * mm, v(505.73, -30.65) * mm, v(506.77, -30.65) * mm]});
            skFitSpline(sketch, "E194", {"points": [v(506.77, -30.65) * mm, v(510.1, -30.65) * mm, v(511.02, -39.58) * mm, v(508.46, -47.01) * mm]});
            skFitSpline(sketch, "E195", {"points": [v(508.46, -47.01) * mm, v(500.27, -70.78) * mm, v(464.23, -93.67) * mm, v(443.63, -88.18) * mm]});
            skFitSpline(sketch, "E196", {"points": [v(443.63, -88.18) * mm, v(436.32, -86.23) * mm, v(430.49, -78.96) * mm, v(428.05, -68.77) * mm]});
            skFitSpline(sketch, "E197", {"points": [v(428.05, -68.77) * mm, v(426, -60.18) * mm, v(425.55, -59.99) * mm, v(418.25, -64.52) * mm]});
            skFitSpline(sketch, "E198", {"points": [v(418.25, -64.52) * mm, v(412.67, -68) * mm, v(408.97, -68.73) * mm, v(397.88, -68.57) * mm]});
            skFitSpline(sketch, "E199", {"points": [v(397.88, -68.57) * mm, v(384.98, -68.4) * mm, v(384.01, -68.68) * mm, v(377.5, -74.64) * mm]});
            skFitSpline(sketch, "E200", {"points": [v(377.5, -74.64) * mm, v(365.8, -85.37) * mm, v(355.8, -89.15) * mm, v(337.98, -89.6) * mm]});
            skFitSpline(sketch, "E201", {"points": [v(337.98, -89.6) * mm, v(329.28, -89.82) * mm, v(320.07, -89.33) * mm, v(317.5, -88.5) * mm]});
            skFitSpline(sketch, "E202", {"points": [v(385.7, -25.43) * mm, v(386.64, -17.46) * mm, v(386.3, -15.64) * mm, v(383.66, -14.63) * mm]});
            skFitSpline(sketch, "E203", {"points": [v(383.66, -14.63) * mm, v(379.08, -12.87) * mm, v(376.38, -16.52) * mm, v(376.67, -24.09) * mm]});
            skFitSpline(sketch, "E204", {"points": [v(376.67, -24.09) * mm, v(376.97, -32.15) * mm, v(380.4, -39.18) * mm, v(382.83, -36.75) * mm]});
            skFitSpline(sketch, "E205", {"points": [v(382.83, -36.75) * mm, v(383.78, -35.8) * mm, v(385.07, -30.7) * mm, v(385.7, -25.43) * mm]});
            skFitSpline(sketch, "E206", {"points": [v(-539.73, 126.1) * mm, v(-551.06, 131.84) * mm, v(-551, 146.27) * mm, v(-539.62, 152.05) * mm]});
            skFitSpline(sketch, "E207", {"points": [v(-539.62, 152.05) * mm, v(-533.86, 154.98) * mm, v(-526.13, 155.3) * mm, v(-462.1, 155.3) * mm]});
            skLineSegment(sketch, "E208", {"start": v(-462.1, 155.3) * mm, "end": v(-390.97, 155.3) * mm});
            skLineSegment(sketch, "E209", {"start": v(-390.97, 155.3) * mm, "end": v(-390.97, 160.85) * mm});
            skFitSpline(sketch, "E210", {"points": [v(-390.97, 160.85) * mm, v(-390.97, 170.05) * mm, v(-385.48, 181.2) * mm, v(-379.4, 184.35) * mm]});
            skFitSpline(sketch, "E211", {"points": [v(-379.4, 184.35) * mm, v(-373.17, 187.57) * mm, v(-10.28, 250.15) * mm, v(2.18, 250.15) * mm]});
            skFitSpline(sketch, "E212", {"points": [v(2.18, 250.15) * mm, v(10.33, 250.15) * mm, v(362.94, 190.41) * mm, v(375.5, 186.9) * mm]});
            skFitSpline(sketch, "E213", {"points": [v(375.5, 186.9) * mm, v(384.93, 184.27) * mm, v(391.52, 175.86) * mm, v(393.02, 164.53) * mm]});
            skLineSegment(sketch, "E214", {"start": v(393.02, 164.53) * mm, "end": v(394.24, 155.3) * mm});
            skLineSegment(sketch, "E215", {"start": v(394.24, 155.3) * mm, "end": v(464.39, 155.3) * mm});
            skFitSpline(sketch, "E216", {"points": [v(464.39, 155.3) * mm, v(536.67, 155.3) * mm, v(544.5, 154.6) * mm, v(548.14, 147.8) * mm]});
            skFitSpline(sketch, "E217", {"points": [v(548.14, 147.8) * mm, v(551.05, 142.36) * mm, v(550.26, 133.77) * mm, v(546.41, 129.02) * mm]});
            skLineSegment(sketch, "E218", {"start": v(546.41, 129.02) * mm, "end": v(542.86, 124.63) * mm});
            skLineSegment(sketch, "E219", {"start": v(542.86, 124.63) * mm, "end": v(3.88, 124.18) * mm});
            skFitSpline(sketch, "E220", {"points": [v(3.88, 124.18) * mm, v(-428.24, 123.83) * mm, v(-536, 124.2) * mm, v(-539.73, 126.1) * mm]});
            skLineSegment(sketch, "E221", {"start": v(-539.73, 126.1) * mm, "end": v(-539.73, 126.1) * mm});
            skSolve(sketch);
        }
        {
            var Q0;
            Q0=makeQuery(id+"F5.opExtrude","CAP_FACE",FACE,{"disambiguationData":[OSD([sQuery(id+"F4.wireOp",EDGE,"E1.bottom"),sQuery(id+"F4.wireOp",EDGE,"E1.top"),sQuery(id+"F4.wireOp",EDGE,"E1.left"),sQuery(id+"F4.wireOp",EDGE,"E1.right")])],"isStart":false});
            var sketch = newSketch(context, id + "F9", { "sketchPlane" : qUnion([Q0])});
            skFitSpline(sketch, "E222", {"points": [v(-4.02, 72.8) * mm, v(-5.86, 73.18) * mm, v(-39.6, 78.99) * mm, v(-78.98, 85.71) * mm]});
            skFitSpline(sketch, "E223", {"points": [v(-78.98, 85.71) * mm, v(-121.51, 92.97) * mm, v(-151.23, 98.37) * mm, v(-152.13, 99) * mm]});
            skFitSpline(sketch, "E224", {"points": [v(-152.13, 99) * mm, v(-154.65, 100.77) * mm, v(-155.8, 102.96) * mm, v(-156.27, 106.9) * mm]});
            skLineSegment(sketch, "E225", {"start": v(-156.27, 106.9) * mm, "end": v(-156.7, 110.63) * mm});
            skLineSegment(sketch, "E226", {"start": v(-156.7, 110.63) * mm, "end": v(-185.43, 110.64) * mm});
            skFitSpline(sketch, "E227", {"points": [v(-185.43, 110.64) * mm, v(-216.4, 110.65) * mm, v(-217, 110.72) * mm, v(-218.85, 114.58) * mm]});
            skFitSpline(sketch, "E228", {"points": [v(-218.85, 114.58) * mm, v(-220.24, 117.49) * mm, v(-219.12, 120.37) * mm, v(-215.96, 121.97) * mm]});
            skFitSpline(sketch, "E229", {"points": [v(-215.96, 121.97) * mm, v(-213.54, 123.2) * mm, v(-201.69, 123.27) * mm, v(0.15, 123.27) * mm]});
            skFitSpline(sketch, "E230", {"points": [v(0.15, 123.27) * mm, v(154.15, 123.27) * mm, v(214.36, 123.04) * mm, v(216.06, 122.45) * mm]});
            skFitSpline(sketch, "E231", {"points": [v(216.06, 122.45) * mm, v(217.36, 122) * mm, v(218.75, 121.02) * mm, v(219.15, 120.27) * mm]});
            skFitSpline(sketch, "E232", {"points": [v(219.15, 120.27) * mm, v(220.3, 118.1) * mm, v(220, 114.66) * mm, v(218.45, 112.76) * mm]});
            skLineSegment(sketch, "E233", {"start": v(218.45, 112.76) * mm, "end": v(217.03, 111) * mm});
            skLineSegment(sketch, "E234", {"start": v(217.03, 111) * mm, "end": v(187.03, 110.63) * mm});
            skLineSegment(sketch, "E235", {"start": v(187.03, 110.63) * mm, "end": v(157.02, 110.26) * mm});
            skLineSegment(sketch, "E236", {"start": v(157.02, 110.26) * mm, "end": v(156.89, 107.16) * mm});
            skFitSpline(sketch, "E237", {"points": [v(156.89, 107.16) * mm, v(156.68, 102.47) * mm, v(154.96, 99.8) * mm, v(151.27, 98.44) * mm]});
            skFitSpline(sketch, "E238", {"points": [v(151.27, 98.44) * mm, v(148.68, 97.48) * mm, v(0.92, 71.75) * mm, v(-0.3, 72.04) * mm]});
            skFitSpline(sketch, "E239", {"points": [v(-0.3, 72.04) * mm, v(-0.5, 72.09) * mm, v(-2.18, 72.43) * mm, v(-4.02, 72.8) * mm]});
            skLineSegment(sketch, "E240", {"start": v(-4.02, 72.8) * mm, "end": v(-4.02, 72.8) * mm});
            skFitSpline(sketch, "E241", {"points": [v(65.16, 135.44) * mm, v(57.71, 137.18) * mm, v(51.02, 139.75) * mm, v(47.2, 142.32) * mm]});
            skLineSegment(sketch, "E242", {"start": v(47.2, 142.32) * mm, "end": v(43.41, 144.86) * mm});
            skLineSegment(sketch, "E243", {"start": v(43.41, 144.86) * mm, "end": v(40.57, 142.3) * mm});
            skFitSpline(sketch, "E244", {"points": [v(40.57, 142.3) * mm, v(37.06, 139.12) * mm, v(34.31, 137.67) * mm, v(29.98, 136.7) * mm]});
            skFitSpline(sketch, "E245", {"points": [v(29.98, 136.7) * mm, v(21.03, 134.7) * mm, v(17.62, 141.67) * mm, v(20.1, 156.92) * mm]});
            skFitSpline(sketch, "E246", {"points": [v(20.1, 156.92) * mm, v(21.74, 167.04) * mm, v(21.67, 168.5) * mm, v(19.44, 169.51) * mm]});
            skFitSpline(sketch, "E247", {"points": [v(19.44, 169.51) * mm, v(16.97, 170.64) * mm, v(14.54, 169) * mm, v(11.84, 164.39) * mm]});
            skFitSpline(sketch, "E248", {"points": [v(11.84, 164.39) * mm, v(8.3, 158.34) * mm, v(7.26, 154.32) * mm, v(8.1, 149.86) * mm]});
            skFitSpline(sketch, "E249", {"points": [v(8.1, 149.86) * mm, v(8.5, 147.71) * mm, v(8.87, 144.64) * mm, v(8.92, 143.03) * mm]});
            skFitSpline(sketch, "E250", {"points": [v(8.92, 143.03) * mm, v(9, 140.4) * mm, v(8.69, 139.88) * mm, v(5.87, 137.89) * mm]});
            skFitSpline(sketch, "E251", {"points": [v(5.87, 137.89) * mm, v(1.64, 134.9) * mm, v(-3.13, 134.68) * mm, v(-4.53, 137.4) * mm]});
            skFitSpline(sketch, "E252", {"points": [v(-4.53, 137.4) * mm, v(-5.7, 139.68) * mm, v(-5.78, 149.47) * mm, v(-4.73, 161.2) * mm]});
            skFitSpline(sketch, "E253", {"points": [v(-4.73, 161.2) * mm, v(-3.79, 171.71) * mm, v(-4.05, 173.1) * mm, v(-6.94, 173.1) * mm]});
            skFitSpline(sketch, "E254", {"points": [v(-6.94, 173.1) * mm, v(-9.67, 173.1) * mm, v(-12.3, 170.1) * mm, v(-15.66, 163.09) * mm]});
            skFitSpline(sketch, "E255", {"points": [v(-15.66, 163.09) * mm, v(-18.48, 157.2) * mm, v(-18.76, 153.85) * mm, v(-17.02, 146.47) * mm]});
            skFitSpline(sketch, "E256", {"points": [v(-17.02, 146.47) * mm, v(-15.68, 140.78) * mm, v(-16.07, 139.86) * mm, v(-20.99, 137.18) * mm]});
            skFitSpline(sketch, "E257", {"points": [v(-20.99, 137.18) * mm, v(-27.42, 133.68) * mm, v(-30.19, 134.83) * mm, v(-31.13, 141.4) * mm]});
            skLineSegment(sketch, "E258", {"start": v(-31.13, 141.4) * mm, "end": v(-31.66, 145.04) * mm});
            skLineSegment(sketch, "E259", {"start": v(-31.66, 145.04) * mm, "end": v(-34.76, 142.05) * mm});
            skFitSpline(sketch, "E260", {"points": [v(-34.76, 142.05) * mm, v(-38.93, 138.02) * mm, v(-42.08, 136.56) * mm, v(-46.82, 136.45) * mm]});
            skFitSpline(sketch, "E261", {"points": [v(-46.82, 136.45) * mm, v(-51.45, 136.34) * mm, v(-53.29, 137.58) * mm, v(-55.43, 142.24) * mm]});
            skFitSpline(sketch, "E262", {"points": [v(-55.43, 142.24) * mm, v(-57.76, 147.32) * mm, v(-56.74, 159.36) * mm, v(-53.44, 165.75) * mm]});
            skLineSegment(sketch, "E263", {"start": v(-53.44, 165.75) * mm, "end": v(-52.29, 167.98) * mm});
            skLineSegment(sketch, "E264", {"start": v(-52.29, 167.98) * mm, "end": v(-56.59, 167.76) * mm});
            skLineSegment(sketch, "E265", {"start": v(-56.59, 167.76) * mm, "end": v(-60.89, 167.53) * mm});
            skLineSegment(sketch, "E266", {"start": v(-60.89, 167.53) * mm, "end": v(-62.25, 161.95) * mm});
            skFitSpline(sketch, "E267", {"points": [v(-62.25, 161.95) * mm, v(-63.3, 157.62) * mm, v(-63.52, 154.56) * mm, v(-63.24, 148.25) * mm]});
            skFitSpline(sketch, "E268", {"points": [v(-63.24, 148.25) * mm, v(-63.03, 143.64) * mm, v(-63.18, 139.53) * mm, v(-63.59, 138.77) * mm]});
            skFitSpline(sketch, "E269", {"points": [v(-63.59, 138.77) * mm, v(-64.61, 136.85) * mm, v(-68.2, 135.17) * mm, v(-71.28, 135.17) * mm]});
            skFitSpline(sketch, "E270", {"points": [v(-71.28, 135.17) * mm, v(-74.54, 135.17) * mm, v(-75.88, 137) * mm, v(-76.6, 142.43) * mm]});
            skLineSegment(sketch, "E271", {"start": v(-76.6, 142.43) * mm, "end": v(-77.1, 146.34) * mm});
            skLineSegment(sketch, "E272", {"start": v(-77.1, 146.34) * mm, "end": v(-80.28, 143.42) * mm});
            skFitSpline(sketch, "E273", {"points": [v(-80.28, 143.42) * mm, v(-84.07, 139.93) * mm, v(-88.18, 137.72) * mm, v(-92.86, 136.67) * mm]});
            skFitSpline(sketch, "E274", {"points": [v(-92.86, 136.67) * mm, v(-97.59, 135.61) * mm, v(-100.15, 136.99) * mm, v(-101.87, 141.51) * mm]});
            skLineSegment(sketch, "E275", {"start": v(-101.87, 141.51) * mm, "end": v(-103.17, 144.9) * mm});
            skLineSegment(sketch, "E276", {"start": v(-103.17, 144.9) * mm, "end": v(-105.29, 142.34) * mm});
            skFitSpline(sketch, "E277", {"points": [v(-105.29, 142.34) * mm, v(-111.87, 134.36) * mm, v(-126.66, 133.64) * mm, v(-132.85, 141) * mm]});
            skFitSpline(sketch, "E278", {"points": [v(-132.85, 141) * mm, v(-135.78, 144.48) * mm, v(-136.68, 148.03) * mm, v(-136.17, 154.08) * mm]});
            skFitSpline(sketch, "E279", {"points": [v(-136.17, 154.08) * mm, v(-135.36, 163.6) * mm, v(-131.77, 171.23) * mm, v(-125.36, 177.03) * mm]});
            skFitSpline(sketch, "E280", {"points": [v(-125.36, 177.03) * mm, v(-119.29, 182.5) * mm, v(-110.9, 185.05) * mm, v(-104, 183.5) * mm]});
            skFitSpline(sketch, "E281", {"points": [v(-104, 183.5) * mm, v(-101.13, 182.87) * mm, v(-100.3, 182.93) * mm, v(-99.25, 183.87) * mm]});
            skFitSpline(sketch, "E282", {"points": [v(-99.25, 183.87) * mm, v(-96.48, 186.38) * mm, v(-90.9, 184.1) * mm, v(-88.4, 179.46) * mm]});
            skLineSegment(sketch, "E283", {"start": v(-88.4, 179.46) * mm, "end": v(-87, 176.85) * mm});
            skLineSegment(sketch, "E284", {"start": v(-87, 176.85) * mm, "end": v(-89.4, 171.99) * mm});
            skFitSpline(sketch, "E285", {"points": [v(-89.4, 171.99) * mm, v(-91.68, 167.35) * mm, v(-91.79, 166.74) * mm, v(-91.78, 158.4) * mm]});
            skFitSpline(sketch, "E286", {"points": [v(-91.78, 158.4) * mm, v(-91.76, 148.82) * mm, v(-91.35, 147.39) * mm, v(-88.84, 148.18) * mm]});
            skFitSpline(sketch, "E287", {"points": [v(-88.84, 148.18) * mm, v(-86.14, 149.04) * mm, v(-75.42, 159.87) * mm, v(-75.42, 161.74) * mm]});
            skFitSpline(sketch, "E288", {"points": [v(-75.42, 161.74) * mm, v(-75.42, 162.64) * mm, v(-74.6, 165.64) * mm, v(-73.6, 168.41) * mm]});
            skFitSpline(sketch, "E289", {"points": [v(-73.6, 168.41) * mm, v(-71.82, 173.31) * mm, v(-71.8, 173.5) * mm, v(-73.13, 174.95) * mm]});
            skFitSpline(sketch, "E290", {"points": [v(-73.13, 174.95) * mm, v(-75.5, 177.57) * mm, v(-76.32, 179.85) * mm, v(-75.83, 182.46) * mm]});
            skFitSpline(sketch, "E291", {"points": [v(-75.83, 182.46) * mm, v(-75.24, 185.64) * mm, v(-72.96, 187.24) * mm, v(-69.04, 187.24) * mm]});
            skFitSpline(sketch, "E292", {"points": [v(-69.04, 187.24) * mm, v(-65.37, 187.24) * mm, v(-62.6, 184.92) * mm, v(-60.4, 180) * mm]});
            skFitSpline(sketch, "E293", {"points": [v(-60.4, 180) * mm, v(-59.19, 177.28) * mm, v(-58.67, 176.83) * mm, v(-56.73, 176.83) * mm]});
            skFitSpline(sketch, "E294", {"points": [v(-56.73, 176.83) * mm, v(-55.5, 176.83) * mm, v(-52.27, 177.71) * mm, v(-49.58, 178.8) * mm]});
            skFitSpline(sketch, "E295", {"points": [v(-49.58, 178.8) * mm, v(-43.83, 181.09) * mm, v(-43.08, 180.85) * mm, v(-40.6, 175.9) * mm]});
            skLineSegment(sketch, "E296", {"start": v(-40.6, 175.9) * mm, "end": v(-38.86, 172.45) * mm});
            skLineSegment(sketch, "E297", {"start": v(-38.86, 172.45) * mm, "end": v(-41.95, 161.2) * mm});
            skFitSpline(sketch, "E298", {"points": [v(-41.95, 161.2) * mm, v(-46.22, 145.7) * mm, v(-45.52, 144.63) * mm, v(-36.56, 153) * mm]});
            skLineSegment(sketch, "E299", {"start": v(-36.56, 153) * mm, "end": v(-31.01, 158.17) * mm});
            skLineSegment(sketch, "E300", {"start": v(-31.01, 158.17) * mm, "end": v(-30.57, 162.9) * mm});
            skFitSpline(sketch, "E301", {"points": [v(-30.57, 162.9) * mm, v(-30.02, 168.87) * mm, v(-27.58, 176.33) * mm, v(-24.53, 181.43) * mm]});
            skFitSpline(sketch, "E302", {"points": [v(-24.53, 181.43) * mm, v(-22.6, 184.65) * mm, v(-21.74, 185.42) * mm, v(-19.9, 185.6) * mm]});
            skFitSpline(sketch, "E303", {"points": [v(-19.9, 185.6) * mm, v(-18.1, 185.79) * mm, v(-17.17, 185.3) * mm, v(-15.37, 183.26) * mm]});
            skFitSpline(sketch, "E304", {"points": [v(-15.37, 183.26) * mm, v(-14.13, 181.85) * mm, v(-12.97, 180.27) * mm, v(-12.8, 179.76) * mm]});
            skFitSpline(sketch, "E305", {"points": [v(-12.8, 179.76) * mm, v(-12.6, 179.14) * mm, v(-11.46, 179.59) * mm, v(-9.31, 181.14) * mm]});
            skFitSpline(sketch, "E306", {"points": [v(-9.31, 181.14) * mm, v(-4.9, 184.34) * mm, v(-0.58, 184.9) * mm, v(3.7, 182.82) * mm]});
            skFitSpline(sketch, "E307", {"points": [v(3.7, 182.82) * mm, v(7.18, 181.14) * mm, v(8.97, 179.06) * mm, v(9.8, 175.74) * mm]});
            skLineSegment(sketch, "E308", {"start": v(9.8, 175.74) * mm, "end": v(10.3, 173.75) * mm});
            skLineSegment(sketch, "E309", {"start": v(10.3, 173.75) * mm, "end": v(12.25, 175.62) * mm});
            skFitSpline(sketch, "E310", {"points": [v(12.25, 175.62) * mm, v(17.33, 180.47) * mm, v(26.31, 182.02) * mm, v(31, 178.85) * mm]});
            skFitSpline(sketch, "E311", {"points": [v(31, 178.85) * mm, v(32.4, 177.92) * mm, v(33.94, 176.33) * mm, v(34.45, 175.32) * mm]});
            skFitSpline(sketch, "E312", {"points": [v(34.45, 175.32) * mm, v(35.9, 172.45) * mm, v(35.57, 166) * mm, v(33.55, 157.63) * mm]});
            skFitSpline(sketch, "E313", {"points": [v(33.55, 157.63) * mm, v(32.52, 153.4) * mm, v(31.69, 149.48) * mm, v(31.69, 148.89) * mm]});
            skFitSpline(sketch, "E314", {"points": [v(31.69, 148.89) * mm, v(31.69, 146.54) * mm, v(34.4, 148.1) * mm, v(40.28, 153.85) * mm]});
            skFitSpline(sketch, "E315", {"points": [v(40.28, 153.85) * mm, v(44.14, 157.62) * mm, v(46.79, 159.67) * mm, v(47.35, 159.33) * mm]});
            skFitSpline(sketch, "E316", {"points": [v(47.35, 159.33) * mm, v(47.95, 158.95) * mm, v(48.11, 157.38) * mm, v(47.84, 154.41) * mm]});
            skFitSpline(sketch, "E317", {"points": [v(47.84, 154.41) * mm, v(47.47, 150.27) * mm, v(47.53, 150.05) * mm, v(49.13, 150.05) * mm]});
            skFitSpline(sketch, "E318", {"points": [v(49.13, 150.05) * mm, v(50.7, 150.05) * mm, v(50.83, 150.44) * mm, v(51.25, 156.19) * mm]});
            skFitSpline(sketch, "E319", {"points": [v(51.25, 156.19) * mm, v(52.17, 169.14) * mm, v(59.1, 189.49) * mm, v(64.13, 194.01) * mm]});
            skFitSpline(sketch, "E320", {"points": [v(64.13, 194.01) * mm, v(71.1, 200.3) * mm, v(71.85, 195.23) * mm, v(67.26, 173.1) * mm]});
            skFitSpline(sketch, "E321", {"points": [v(67.26, 173.1) * mm, v(65.38, 164.06) * mm, v(63.36, 146.58) * mm, v(64.09, 145.7) * mm]});
            skFitSpline(sketch, "E322", {"points": [v(64.09, 145.7) * mm, v(64.6, 145.1) * mm, v(70.27, 144.14) * mm, v(73.34, 144.12) * mm]});
            skFitSpline(sketch, "E323", {"points": [v(73.34, 144.12) * mm, v(80.28, 144.1) * mm, v(86.16, 147.32) * mm, v(88.22, 152.3) * mm]});
            skFitSpline(sketch, "E324", {"points": [v(88.22, 152.3) * mm, v(89.7, 155.84) * mm, v(88.86, 165.57) * mm, v(86.8, 168.9) * mm]});
            skFitSpline(sketch, "E325", {"points": [v(86.8, 168.9) * mm, v(85.14, 171.6) * mm, v(85.07, 171.62) * mm, v(80.14, 171.62) * mm]});
            skFitSpline(sketch, "E326", {"points": [v(80.14, 171.62) * mm, v(74.8, 171.62) * mm, v(72.33, 172.7) * mm, v(71.64, 175.32) * mm]});
            skFitSpline(sketch, "E327", {"points": [v(71.64, 175.32) * mm, v(71.42, 176.18) * mm, v(71.81, 177.53) * mm, v(72.57, 178.46) * mm]});
            skFitSpline(sketch, "E328", {"points": [v(72.57, 178.46) * mm, v(73.65, 179.8) * mm, v(74.91, 180.16) * mm, v(79.74, 180.5) * mm]});
            skFitSpline(sketch, "E329", {"points": [v(79.74, 180.5) * mm, v(85.34, 180.9) * mm, v(85.65, 181.02) * mm, v(86.7, 183.15) * mm]});
            skFitSpline(sketch, "E330", {"points": [v(86.7, 183.15) * mm, v(87.3, 184.38) * mm, v(87.8, 187.4) * mm, v(87.8, 189.85) * mm]});
            skFitSpline(sketch, "E331", {"points": [v(87.8, 189.85) * mm, v(87.81, 197.65) * mm, v(84.36, 200.65) * mm, v(74.71, 201.22) * mm]});
            skFitSpline(sketch, "E332", {"points": [v(74.71, 201.22) * mm, v(67.9, 201.62) * mm, v(62.96, 200.56) * mm, v(55.88, 197.17) * mm]});
            skFitSpline(sketch, "E333", {"points": [v(55.88, 197.17) * mm, v(49.82, 194.26) * mm, v(47.3, 193.97) * mm, v(47.3, 196.18) * mm]});
            skFitSpline(sketch, "E334", {"points": [v(47.3, 196.18) * mm, v(47.3, 200.18) * mm, v(57.13, 207.33) * mm, v(66.24, 209.96) * mm]});
            skFitSpline(sketch, "E335", {"points": [v(66.24, 209.96) * mm, v(72.35, 211.72) * mm, v(84.52, 211.15) * mm, v(90.82, 208.8) * mm]});
            skFitSpline(sketch, "E336", {"points": [v(90.82, 208.8) * mm, v(96.65, 206.62) * mm, v(101.76, 201.55) * mm, v(102.97, 196.71) * mm]});
            skFitSpline(sketch, "E337", {"points": [v(102.97, 196.71) * mm, v(104.88, 189.14) * mm, v(103.62, 184.53) * mm, v(98.2, 179.25) * mm]});
            skFitSpline(sketch, "E338", {"points": [v(98.2, 179.25) * mm, v(96, 177.1) * mm, v(94.48, 175.34) * mm, v(94.82, 175.34) * mm]});
            skFitSpline(sketch, "E339", {"points": [v(94.82, 175.34) * mm, v(96.3, 175.34) * mm, v(102.36, 169.1) * mm, v(103.81, 166.1) * mm]});
            skFitSpline(sketch, "E340", {"points": [v(103.81, 166.1) * mm, v(106.07, 161.42) * mm, v(106.16, 152.36) * mm, v(103.99, 148.1) * mm]});
            skFitSpline(sketch, "E341", {"points": [v(103.99, 148.1) * mm, v(101.64, 143.52) * mm, v(95.7, 138.56) * mm, v(90.26, 136.67) * mm]});
            skFitSpline(sketch, "E342", {"points": [v(90.26, 136.67) * mm, v(84.46, 134.65) * mm, v(71.3, 134) * mm, v(65.16, 135.44) * mm]});
            skFitSpline(sketch, "E343", {"points": [v(-112.85, 147.12) * mm, v(-107.25, 149.24) * mm, v(-103.73, 155.26) * mm, v(-103.7, 162.75) * mm]});
            skFitSpline(sketch, "E344", {"points": [v(-103.7, 162.75) * mm, v(-103.7, 165.43) * mm, v(-103.33, 169.57) * mm, v(-102.9, 171.93) * mm]});
            skFitSpline(sketch, "E345", {"points": [v(-102.9, 171.93) * mm, v(-102.46, 174.3) * mm, v(-102.28, 176.41) * mm, v(-102.5, 176.64) * mm]});
            skFitSpline(sketch, "E346", {"points": [v(-102.5, 176.64) * mm, v(-103.28, 177.42) * mm, v(-109.7, 174.44) * mm, v(-113.2, 171.68) * mm]});
            skFitSpline(sketch, "E347", {"points": [v(-113.2, 171.68) * mm, v(-118.2, 167.72) * mm, v(-120.95, 162.32) * mm, v(-121.38, 155.55) * mm]});
            skFitSpline(sketch, "E348", {"points": [v(-121.38, 155.55) * mm, v(-121.7, 150.53) * mm, v(-121.6, 150.04) * mm, v(-119.8, 148.25) * mm]});
            skFitSpline(sketch, "E349", {"points": [v(-119.8, 148.25) * mm, v(-117.72, 146.17) * mm, v(-116.09, 145.9) * mm, v(-112.85, 147.12) * mm]});
            skFitSpline(sketch, "E350", {"points": [v(-183.84, 136) * mm, v(-185.9, 138.13) * mm, v(-184.4, 157.8) * mm, v(-181.44, 167.09) * mm]});
            skFitSpline(sketch, "E351", {"points": [v(-181.44, 167.09) * mm, v(-180.97, 168.57) * mm, v(-181.2, 168.65) * mm, v(-186.2, 168.65) * mm]});
            skFitSpline(sketch, "E352", {"points": [v(-186.2, 168.65) * mm, v(-190.78, 168.65) * mm, v(-191.46, 168.82) * mm, v(-191.46, 170) * mm]});
            skFitSpline(sketch, "E353", {"points": [v(-191.46, 170) * mm, v(-191.46, 172.08) * mm, v(-187.7, 175.19) * mm, v(-182.96, 177.03) * mm]});
            skLineSegment(sketch, "E354", {"start": v(-182.96, 177.03) * mm, "end": v(-178.64, 178.7) * mm});
            skLineSegment(sketch, "E355", {"start": v(-178.64, 178.7) * mm, "end": v(-175.48, 187.62) * mm});
            skFitSpline(sketch, "E356", {"points": [v(-175.48, 187.62) * mm, v(-173.75, 192.53) * mm, v(-172.06, 197.16) * mm, v(-171.74, 197.93) * mm]});
            skFitSpline(sketch, "E357", {"points": [v(-171.74, 197.93) * mm, v(-171.2, 199.2) * mm, v(-171.42, 199.27) * mm, v(-174.43, 198.78) * mm]});
            skFitSpline(sketch, "E358", {"points": [v(-174.43, 198.78) * mm, v(-179.3, 198) * mm, v(-183.51, 195.92) * mm, v(-187.21, 192.52) * mm]});
            skFitSpline(sketch, "E359", {"points": [v(-187.21, 192.52) * mm, v(-191.98, 188.12) * mm, v(-193.7, 188.58) * mm, v(-193.7, 194.26) * mm]});
            skFitSpline(sketch, "E360", {"points": [v(-193.7, 194.26) * mm, v(-193.7, 199.51) * mm, v(-187.2, 205.3) * mm, v(-178.22, 208.08) * mm]});
            skFitSpline(sketch, "E361", {"points": [v(-178.22, 208.08) * mm, v(-170.95, 210.33) * mm, v(-162.53, 210.91) * mm, v(-143.6, 210.48) * mm]});
            skFitSpline(sketch, "E362", {"points": [v(-143.6, 210.48) * mm, v(-124.58, 210.05) * mm, v(-124.9, 210.15) * mm, v(-127.15, 204.87) * mm]});
            skFitSpline(sketch, "E363", {"points": [v(-127.15, 204.87) * mm, v(-129.57, 199.2) * mm, v(-129.71, 199.15) * mm, v(-144.5, 199.13) * mm]});
            skLineSegment(sketch, "E364", {"start": v(-144.5, 199.13) * mm, "end": v(-157.62, 199.12) * mm});
            skLineSegment(sketch, "E365", {"start": v(-157.62, 199.12) * mm, "end": v(-159.58, 191.14) * mm});
            skFitSpline(sketch, "E366", {"points": [v(-159.58, 191.14) * mm, v(-160.65, 186.74) * mm, v(-161.66, 182.65) * mm, v(-161.8, 182.04) * mm]});
            skFitSpline(sketch, "E367", {"points": [v(-161.8, 182.04) * mm, v(-162.04, 181.1) * mm, v(-160.6, 180.89) * mm, v(-152.8, 180.7) * mm]});
            skFitSpline(sketch, "E368", {"points": [v(-152.8, 180.7) * mm, v(-146.97, 180.58) * mm, v(-143.35, 180.2) * mm, v(-143.02, 179.66) * mm]});
            skFitSpline(sketch, "E369", {"points": [v(-143.02, 179.66) * mm, v(-142.41, 178.68) * mm, v(-144.07, 172.79) * mm, v(-145.4, 171.17) * mm]});
            skFitSpline(sketch, "E370", {"points": [v(-145.4, 171.17) * mm, v(-146.2, 170.23) * mm, v(-147.83, 170.13) * mm, v(-155.74, 170.56) * mm]});
            skLineSegment(sketch, "E371", {"start": v(-155.74, 170.56) * mm, "end": v(-165.13, 171.07) * mm});
            skLineSegment(sketch, "E372", {"start": v(-165.13, 171.07) * mm, "end": v(-166.72, 164.47) * mm});
            skFitSpline(sketch, "E373", {"points": [v(-166.72, 164.47) * mm, v(-168.53, 156.92) * mm, v(-169.62, 150.4) * mm, v(-170.3, 143.15) * mm]});
            skFitSpline(sketch, "E374", {"points": [v(-170.3, 143.15) * mm, v(-170.69, 138.84) * mm, v(-171.03, 137.92) * mm, v(-172.64, 136.87) * mm]});
            skFitSpline(sketch, "E375", {"points": [v(-172.64, 136.87) * mm, v(-175.08, 135.27) * mm, v(-182.56, 134.7) * mm, v(-183.84, 136) * mm]});
            skFitSpline(sketch, "E376", {"points": [v(126.9, 136.58) * mm, v(121.05, 138.46) * mm, v(115.7, 143.46) * mm, v(114.21, 148.4) * mm]});
            skFitSpline(sketch, "E377", {"points": [v(114.21, 148.4) * mm, v(112.76, 153.26) * mm, v(113.59, 163.12) * mm, v(115.87, 168.03) * mm]});
            skFitSpline(sketch, "E378", {"points": [v(115.87, 168.03) * mm, v(119.6, 176.03) * mm, v(126.32, 181.7) * mm, v(134.25, 183.54) * mm]});
            skFitSpline(sketch, "E379", {"points": [v(134.25, 183.54) * mm, v(141.52, 185.22) * mm, v(151.26, 183.23) * mm, v(154.42, 179.43) * mm]});
            skFitSpline(sketch, "E380", {"points": [v(154.42, 179.43) * mm, v(155.9, 177.65) * mm, v(154.6, 177.1) * mm, v(147.83, 176.64) * mm]});
            skFitSpline(sketch, "E381", {"points": [v(147.83, 176.64) * mm, v(144.69, 176.43) * mm, v(140.93, 175.75) * mm, v(139.47, 175.14) * mm]});
            skFitSpline(sketch, "E382", {"points": [v(139.47, 175.14) * mm, v(132.67, 172.3) * mm, v(128.2, 165.5) * mm, v(128.1, 157.86) * mm]});
            skFitSpline(sketch, "E383", {"points": [v(128.1, 157.86) * mm, v(127.97, 148.8) * mm, v(133.7, 144.61) * mm, v(142.75, 147.13) * mm]});
            skLineSegment(sketch, "E384", {"start": v(142.75, 147.13) * mm, "end": v(145.58, 147.91) * mm});
            skLineSegment(sketch, "E385", {"start": v(145.58, 147.91) * mm, "end": v(143.02, 150.75) * mm});
            skFitSpline(sketch, "E386", {"points": [v(143.02, 150.75) * mm, v(134.47, 160.22) * mm, v(139.5, 174.6) * mm, v(151.37, 174.6) * mm]});
            skFitSpline(sketch, "E387", {"points": [v(151.37, 174.6) * mm, v(155.58, 174.6) * mm, v(157.91, 173.5) * mm, v(159.66, 170.71) * mm]});
            skFitSpline(sketch, "E388", {"points": [v(159.66, 170.71) * mm, v(160.95, 168.66) * mm, v(161.14, 167.4) * mm, v(160.87, 162.7) * mm]});
            skFitSpline(sketch, "E389", {"points": [v(160.87, 162.7) * mm, v(160.69, 159.63) * mm, v(160.3, 156.36) * mm, v(160, 155.44) * mm]});
            skFitSpline(sketch, "E390", {"points": [v(160, 155.44) * mm, v(159.32, 153.37) * mm, v(160.82, 153.21) * mm, v(164.31, 154.97) * mm]});
            skFitSpline(sketch, "E391", {"points": [v(164.31, 154.97) * mm, v(168.41, 157.05) * mm, v(170.04, 159) * mm, v(170.07, 161.9) * mm]});
            skFitSpline(sketch, "E392", {"points": [v(170.07, 161.9) * mm, v(170.08, 163.36) * mm, v(170.53, 166.81) * mm, v(171.06, 169.57) * mm]});
            skFitSpline(sketch, "E393", {"points": [v(171.06, 169.57) * mm, v(171.6, 172.33) * mm, v(171.86, 174.76) * mm, v(171.66, 174.96) * mm]});
            skFitSpline(sketch, "E394", {"points": [v(171.66, 174.96) * mm, v(171.45, 175.17) * mm, v(170.12, 175.34) * mm, v(168.72, 175.34) * mm]});
            skFitSpline(sketch, "E395", {"points": [v(168.72, 175.34) * mm, v(166.17, 175.34) * mm, v(166.16, 175.36) * mm, v(166.66, 178.04) * mm]});
            skFitSpline(sketch, "E396", {"points": [v(166.66, 178.04) * mm, v(167.46, 182.3) * mm, v(168.56, 183.52) * mm, v(171.6, 183.52) * mm]});
            skFitSpline(sketch, "E397", {"points": [v(171.6, 183.52) * mm, v(174.2, 183.52) * mm, v(174.36, 183.67) * mm, v(175.88, 187.8) * mm]});
            skFitSpline(sketch, "E398", {"points": [v(175.88, 187.8) * mm, v(180.22, 199.6) * mm, v(185.9, 202.36) * mm, v(189.42, 194.38) * mm]});
            skLineSegment(sketch, "E399", {"start": v(189.42, 194.38) * mm, "end": v(190.87, 191.12) * mm});
            skLineSegment(sketch, "E400", {"start": v(190.87, 191.12) * mm, "end": v(189.02, 187.88) * mm});
            skFitSpline(sketch, "E401", {"points": [v(189.02, 187.88) * mm, v(188, 186.1) * mm, v(187.16, 184.39) * mm, v(187.15, 184.08) * mm]});
            skFitSpline(sketch, "E402", {"points": [v(187.15, 184.08) * mm, v(187.15, 183.77) * mm, v(189.49, 183.52) * mm, v(192.35, 183.52) * mm]});
            skFitSpline(sketch, "E403", {"points": [v(192.35, 183.52) * mm, v(197.32, 183.52) * mm, v(197.56, 183.44) * mm, v(197.56, 181.77) * mm]});
            skFitSpline(sketch, "E404", {"points": [v(197.56, 181.77) * mm, v(197.56, 180.81) * mm, v(197.2, 178.97) * mm, v(196.74, 177.68) * mm]});
            skFitSpline(sketch, "E405", {"points": [v(196.74, 177.68) * mm, v(195.93, 175.35) * mm, v(195.92, 175.34) * mm, v(190.5, 175.34) * mm]});
            skFitSpline(sketch, "E406", {"points": [v(190.5, 175.34) * mm, v(186.52, 175.34) * mm, v(184.97, 175.06) * mm, v(184.67, 174.3) * mm]});
            skFitSpline(sketch, "E407", {"points": [v(184.67, 174.3) * mm, v(184.45, 173.72) * mm, v(183.86, 169.28) * mm, v(183.36, 164.44) * mm]});
            skFitSpline(sketch, "E408", {"points": [v(183.36, 164.44) * mm, v(182.36, 154.73) * mm, v(182.85, 148.74) * mm, v(184.7, 148.02) * mm]});
            skFitSpline(sketch, "E409", {"points": [v(184.7, 148.02) * mm, v(186.5, 147.34) * mm, v(192.17, 150.68) * mm, v(197.26, 155.44) * mm]});
            skFitSpline(sketch, "E410", {"points": [v(197.26, 155.44) * mm, v(199.78, 157.8) * mm, v(202.18, 159.72) * mm, v(202.6, 159.72) * mm]});
            skFitSpline(sketch, "E411", {"points": [v(202.6, 159.72) * mm, v(203.93, 159.72) * mm, v(204.3, 156.15) * mm, v(203.27, 153.17) * mm]});
            skFitSpline(sketch, "E412", {"points": [v(203.27, 153.17) * mm, v(200, 143.67) * mm, v(185.58, 134.51) * mm, v(177.34, 136.7) * mm]});
            skFitSpline(sketch, "E413", {"points": [v(177.34, 136.7) * mm, v(174.42, 137.49) * mm, v(172.08, 140.4) * mm, v(171.1, 144.47) * mm]});
            skFitSpline(sketch, "E414", {"points": [v(171.1, 144.47) * mm, v(170.29, 147.9) * mm, v(170.1, 147.99) * mm, v(167.19, 146.17) * mm]});
            skFitSpline(sketch, "E415", {"points": [v(167.19, 146.17) * mm, v(164.96, 144.78) * mm, v(163.48, 144.49) * mm, v(159.04, 144.55) * mm]});
            skFitSpline(sketch, "E416", {"points": [v(159.04, 144.55) * mm, v(153.88, 144.62) * mm, v(153.5, 144.5) * mm, v(150.9, 142.12) * mm]});
            skFitSpline(sketch, "E417", {"points": [v(150.9, 142.12) * mm, v(146.2, 137.83) * mm, v(142.2, 136.32) * mm, v(135.08, 136.14) * mm]});
            skFitSpline(sketch, "E418", {"points": [v(135.08, 136.14) * mm, v(131.6, 136.05) * mm, v(127.92, 136.25) * mm, v(126.9, 136.58) * mm]});
            skFitSpline(sketch, "E419", {"points": [v(154.17, 161.8) * mm, v(154.55, 165) * mm, v(154.4, 165.72) * mm, v(153.35, 166.13) * mm]});
            skFitSpline(sketch, "E420", {"points": [v(153.35, 166.13) * mm, v(151.52, 166.83) * mm, v(150.44, 165.37) * mm, v(150.55, 162.34) * mm]});
            skFitSpline(sketch, "E421", {"points": [v(150.55, 162.34) * mm, v(150.68, 159.12) * mm, v(152.04, 156.3) * mm, v(153.02, 157.28) * mm]});
            skFitSpline(sketch, "E422", {"points": [v(153.02, 157.28) * mm, v(153.4, 157.66) * mm, v(153.92, 159.7) * mm, v(154.17, 161.8) * mm]});
            skFitSpline(sketch, "E423", {"points": [v(-216, 222.42) * mm, v(-220.54, 224.72) * mm, v(-220.51, 230.49) * mm, v(-215.96, 232.8) * mm]});
            skFitSpline(sketch, "E424", {"points": [v(-215.96, 232.8) * mm, v(-213.66, 233.97) * mm, v(-210.56, 234.1) * mm, v(-184.95, 234.1) * mm]});
            skLineSegment(sketch, "E425", {"start": v(-184.95, 234.1) * mm, "end": v(-156.5, 234.1) * mm});
            skLineSegment(sketch, "E426", {"start": v(-156.5, 234.1) * mm, "end": v(-156.5, 236.32) * mm});
            skFitSpline(sketch, "E427", {"points": [v(-156.5, 236.32) * mm, v(-156.5, 240) * mm, v(-154.3, 244.46) * mm, v(-151.87, 245.72) * mm]});
            skFitSpline(sketch, "E428", {"points": [v(-151.87, 245.72) * mm, v(-149.38, 247) * mm, v(-4.22, 272.04) * mm, v(0.76, 272.04) * mm]});
            skFitSpline(sketch, "E429", {"points": [v(0.76, 272.04) * mm, v(4.02, 272.04) * mm, v(145.06, 248.14) * mm, v(150.09, 246.74) * mm]});
            skFitSpline(sketch, "E430", {"points": [v(150.09, 246.74) * mm, v(153.86, 245.69) * mm, v(156.5, 242.32) * mm, v(157.1, 237.8) * mm]});
            skLineSegment(sketch, "E431", {"start": v(157.1, 237.8) * mm, "end": v(157.58, 234.1) * mm});
            skLineSegment(sketch, "E432", {"start": v(157.58, 234.1) * mm, "end": v(185.64, 234.1) * mm});
            skFitSpline(sketch, "E433", {"points": [v(185.64, 234.1) * mm, v(214.56, 234.1) * mm, v(217.69, 233.82) * mm, v(219.15, 231.1) * mm]});
            skFitSpline(sketch, "E434", {"points": [v(219.15, 231.1) * mm, v(220.3, 228.93) * mm, v(220, 225.49) * mm, v(218.45, 223.59) * mm]});
            skLineSegment(sketch, "E435", {"start": v(218.45, 223.59) * mm, "end": v(217.03, 221.83) * mm});
            skLineSegment(sketch, "E436", {"start": v(217.03, 221.83) * mm, "end": v(1.44, 221.65) * mm});
            skFitSpline(sketch, "E437", {"points": [v(1.44, 221.65) * mm, v(-171.4, 221.51) * mm, v(-214.51, 221.66) * mm, v(-216, 222.42) * mm]});
            skLineSegment(sketch, "E438", {"start": v(-216, -140.24) * mm, "end": v(-216, -140.24) * mm});
            skSolve(sketch);
        }
        {
            var Q0;
            Q0=makeQuery(id+"F7.opExtrude","SWEPT_FACE",FACE,{"disambiguationData":[OSD([sQuery(id+"F6.wireOp",EDGE,"E3.right")])]});
            var sketch = newSketch(context, id + "F10", { "sketchPlane" : qUnion([Q0])});
            skLineSegment(sketch, "E439.bottom", {"start": v(-740.05, 101.6) * mm, "end": v(-733.7, 101.6) * mm});
            skLineSegment(sketch, "E439.top", {"start": v(-740.05, 95.25) * mm, "end": v(-733.7, 95.25) * mm});
            skLineSegment(sketch, "E439.left", {"start": v(-740.05, 101.6) * mm, "end": v(-740.05, 95.25) * mm});
            skLineSegment(sketch, "E439.right", {"start": v(-733.7, 101.6) * mm, "end": v(-733.7, 95.25) * mm});
            skLineSegment(sketch, "E440.bottom", {"start": v(-721, 101.6) * mm, "end": v(-727.35, 101.6) * mm});
            skLineSegment(sketch, "E440.top", {"start": v(-721, 95.25) * mm, "end": v(-727.35, 95.25) * mm});
            skLineSegment(sketch, "E440.left", {"start": v(-721, 101.6) * mm, "end": v(-721, 95.25) * mm});
            skLineSegment(sketch, "E440.right", {"start": v(-727.35, 101.6) * mm, "end": v(-727.35, 95.25) * mm});
            skLineSegment(sketch, "E441.bottom", {"start": v(-733.7, 0) * mm, "end": v(-727.35, 0) * mm});
            skLineSegment(sketch, "E441.top", {"start": v(-733.7, 6.35) * mm, "end": v(-727.35, 6.35) * mm});
            skLineSegment(sketch, "E441.left", {"start": v(-733.7, 0) * mm, "end": v(-733.7, 6.35) * mm});
            skLineSegment(sketch, "E441.right", {"start": v(-727.35, 0) * mm, "end": v(-727.35, 6.35) * mm});
            skSolve(sketch);
        }
        {
            var Q0;
            Q0 = qSketchRegion(id + "F10", true);
            extrude(context, id + "F11", {"entities" : qUnion([Q0]), "operationType" : NewBodyOperationType.REMOVE, "endBound" : BoundingType.UP_TO_NEXT, "oppositeDirection" : true, "depth" : 25 * mm, "offsetDistance" : 25 * mm});
        }
        {
            var Q0;
            Q0=makeQuery(id+"F5.opExtrude","SWEPT_FACE",FACE,{"disambiguationData":[OSD([sQuery(id+"F4.wireOp",EDGE,"E1.right")])]});
            var sketch = newSketch(context, id + "F12", { "sketchPlane" : qUnion([Q0])});
            skLineSegment(sketch, "E442.bottom", {"start": v(-1500.05, 101.6) * mm, "end": v(-1493.7, 101.6) * mm});
            skLineSegment(sketch, "E442.top", {"start": v(-1500.05, 95.25) * mm, "end": v(-1493.7, 95.25) * mm});
            skLineSegment(sketch, "E442.left", {"start": v(-1500.05, 101.6) * mm, "end": v(-1500.05, 95.25) * mm});
            skLineSegment(sketch, "E442.right", {"start": v(-1493.7, 101.6) * mm, "end": v(-1493.7, 95.25) * mm});
            skLineSegment(sketch, "E443.bottom", {"start": v(-1481, 101.6) * mm, "end": v(-1487.35, 101.6) * mm});
            skLineSegment(sketch, "E443.top", {"start": v(-1481, 95.25) * mm, "end": v(-1487.35, 95.25) * mm});
            skLineSegment(sketch, "E443.left", {"start": v(-1481, 101.6) * mm, "end": v(-1481, 95.25) * mm});
            skLineSegment(sketch, "E443.right", {"start": v(-1487.35, 101.6) * mm, "end": v(-1487.35, 95.25) * mm});
            skLineSegment(sketch, "E444.bottom", {"start": v(-1493.7, 0) * mm, "end": v(-1487.35, 0) * mm});
            skLineSegment(sketch, "E444.top", {"start": v(-1493.7, 6.35) * mm, "end": v(-1487.35, 6.35) * mm});
            skLineSegment(sketch, "E444.left", {"start": v(-1493.7, 0) * mm, "end": v(-1493.7, 6.35) * mm});
            skLineSegment(sketch, "E444.right", {"start": v(-1487.35, 0) * mm, "end": v(-1487.35, 6.35) * mm});
            skSolve(sketch);
        }
        {
            var Q0;
            Q0=makeQuery(id+"F12.imprint","IMPRINT",FACE,{"disambiguationData":[TD([[makeQuery(id+"F12.imprint","IMPRINT",EDGE,{"derivedFrom":sQuery(id+"F12.wireOp",EDGE,"E442.bottom")}),-1.0]])]});
            var Q1;
            Q1=makeQuery(id+"F12.imprint","IMPRINT",FACE,{"disambiguationData":[TD([[makeQuery(id+"F12.imprint","IMPRINT",EDGE,{"derivedFrom":sQuery(id+"F12.wireOp",EDGE,"E443.bottom")}),-1.0]])]});
            var Q2;
            Q2=makeQuery(id+"F12.imprint","IMPRINT",FACE,{"disambiguationData":[TD([[makeQuery(id+"F12.imprint","IMPRINT",EDGE,{"derivedFrom":sQuery(id+"F12.wireOp",EDGE,"E444.bottom")}),1.0]])]});
            extrude(context, id + "F13", {"entities" : qUnion([Q0, Q1, Q2]), "operationType" : NewBodyOperationType.REMOVE, "endBound" : BoundingType.UP_TO_NEXT, "oppositeDirection" : true, "depth" : 25 * mm, "offsetDistance" : 25 * mm});
        }
        {
            var Q0;
            Q0=makeQuery(id+"F7.opExtrude","CAP_FACE",FACE,{"disambiguationData":[OSD([sQuery(id+"F6.wireOp",EDGE,"E3.bottom"),sQuery(id+"F6.wireOp",EDGE,"E3.top"),sQuery(id+"F6.wireOp",EDGE,"E3.left"),sQuery(id+"F6.wireOp",EDGE,"E3.right")])],"isStart":true});
            var sketch = newSketch(context, id + "F14", { "sketchPlane" : qUnion([Q0])});
            skLineSegment(sketch, "E445.top", {"start": v(-1379.4, 320.8) * mm, "end": v(-1481, 320.8) * mm});
            skLineSegment(sketch, "E445.left", {"start": v(-1379.4, 0) * mm, "end": v(-1379.4, 320.8) * mm});
            skLineSegment(sketch, "E445.right", {"start": v(-1481, -101.6) * mm, "end": v(-1481, 320.8) * mm});
            skLineSegment(sketch, "E446", {"start": v(-1379.4, 0) * mm, "end": v(-1481, -101.6) * mm});
            skSolve(sketch);
        }
        {
            var Q0;
            {var subQ0=sQuery(id+"F14.wireOp",EDGE,"E446");Q0=makeQuery(id+"F14.imprint","IMPRINT",FACE,{"disambiguationData":[TD([[makeQuery(id+"F14.imprint","IMPRINT",EDGE,{"derivedFrom":subQ0}),-1.0]])]});}
            var Q1;
            {var subQ1=makeQuery(id+"F7.opExtrude","CAP_EDGE",EDGE,{"disambiguationData":[OSD([sQuery(id+"F6.wireOp",EDGE,"E3.top")])],"isStart":true});var subQ5=sQuery(id+"F14.wireOp",EDGE,"E445.right");var subQ6=makeQuery(id+"F14.imprint","INTERSECT",VERTEX,{"derivedFrom":[subQ1,subQ5]});Q1=makeQuery(id+"F14.imprint","IMPRINT",FACE,{"disambiguationData":[TD([[makeQuery(id+"F14.imprint","IMPRINT",EDGE,{"disambiguationData":[TD([[subQ6,1.0]])],"derivedFrom":subQ1}),-1.0]])]});}
            var Q2;
            {var subQ0=sQuery(id+"F14.wireOp",EDGE,"E445.top");Q2=makeQuery(id+"F14.imprint","IMPRINT",FACE,{"disambiguationData":[TD([[makeQuery(id+"F14.imprint","IMPRINT",EDGE,{"derivedFrom":subQ0}),1.0]])]});}
            extrude(context, id + "F15", {"entities" : qUnion([Q0, Q1, Q2]), "depth" : 19.05 * mm, "offsetDistance" : 25 * mm});
        }
        {
            var Q0;
            Q0=qCreatedBy(makeId("Top.planeOp"),FACE);
            var sketch = newSketch(context, id + "F16", { "sketchPlane" : qUnion([Q0])});
            skLineSegment(sketch, "E447.bottom", {"start": v(-1462, 0) * mm, "end": v(1462, 0) * mm});
            skLineSegment(sketch, "E447.top", {"start": v(-1379.4, -101.6) * mm, "end": v(-101.6, -101.6) * mm});
            skLineSegment(sketch, "E447.left", {"start": v(-1462, 0) * mm, "end": v(-1462, -82.6) * mm});
            skLineSegment(sketch, "E447.right", {"start": v(1462, 0) * mm, "end": v(1462, -82.6) * mm});
            skPoint(sketch, "E448", {"position": v(0, 0) * mm});
            skLineSegment(sketch, "E449.top", {"start": v(-101.6, -82.55) * mm, "end": v(101.6, -82.55) * mm});
            skLineSegment(sketch, "E449.left", {"start": v(-101.6, -101.6) * mm, "end": v(-101.6, -82.55) * mm});
            skLineSegment(sketch, "E449.right", {"start": v(101.6, -101.6) * mm, "end": v(101.6, -82.55) * mm});
            skPoint(sketch, "E450", {"position": v(0, -82.55) * mm});
            skLineSegment(sketch, "E451.trimOffspring", {"start": v(101.6, -101.6) * mm, "end": v(1379.4, -101.6) * mm});
            skLineSegment(sketch, "E452.top", {"start": v(-1462, -82.6) * mm, "end": v(-1379.4, -82.6) * mm});
            skLineSegment(sketch, "E452.right", {"start": v(-1379.4, -101.6) * mm, "end": v(-1379.4, -82.6) * mm});
            skLineSegment(sketch, "E453.top", {"start": v(1462, -82.6) * mm, "end": v(1379.4, -82.6) * mm});
            skLineSegment(sketch, "E453.right", {"start": v(1379.4, -101.6) * mm, "end": v(1379.4, -82.6) * mm});
            skSolve(sketch);
        }
        {
            var Q0;
            Q0 = qSketchRegion(id + "F16", true);
            extrude(context, id + "F17", {"entities" : qUnion([Q0]), "depth" : 19 * mm, "offsetDistance" : 25 * mm});
        }
        {
            var Q0;
            Q0=qCreatedBy(makeId("Top.planeOp"),FACE);
            var sketch = newSketch(context, id + "F18", { "sketchPlane" : qUnion([Q0])});
            skLineSegment(sketch, "E454.bottom", {"start": v(-1682.6, -702) * mm, "end": v(-1600, -702) * mm});
            skLineSegment(sketch, "E454.top", {"start": v(-1682.6, 702) * mm, "end": v(-1600, 702) * mm});
            skLineSegment(sketch, "E454.left", {"start": v(-1701.6, -600.4) * mm, "end": v(-1701.6, 600.4) * mm});
            skLineSegment(sketch, "E454.right", {"start": v(-1600, -702) * mm, "end": v(-1600, 702) * mm});
            skPoint(sketch, "E455", {"position": v(-1600, 0) * mm});
            skLineSegment(sketch, "E456.top", {"start": v(-1701.6, 600.4) * mm, "end": v(-1682.6, 600.4) * mm});
            skLineSegment(sketch, "E456.right", {"start": v(-1682.6, 702) * mm, "end": v(-1682.6, 600.4) * mm});
            skLineSegment(sketch, "E457.top", {"start": v(-1701.6, -600.4) * mm, "end": v(-1682.6, -600.4) * mm});
            skLineSegment(sketch, "E457.right", {"start": v(-1682.6, -702) * mm, "end": v(-1682.6, -600.4) * mm});
            skSolve(sketch);
        }
        {
            var Q0;
            Q0=makeQuery(id+"F18.imprint","IMPRINT",FACE,{"disambiguationData":[TD([[makeQuery(id+"F18.imprint","IMPRINT",EDGE,{"derivedFrom":sQuery(id+"F18.wireOp",EDGE,"E454.bottom")}),1.0]])]});
            extrude(context, id + "F19", {"entities" : qUnion([Q0]), "depth" : 19 * mm, "offsetDistance" : 25 * mm});
        }
        {
            var Q0;
            Q0=qCreatedBy(makeId("Right.planeOp"),FACE);
            var sketch = newSketch(context, id + "F20", { "sketchPlane" : qUnion([Q0])});
            skLineSegment(sketch, "E458.bottom", {"start": v(0, 404.31) * mm, "end": v(101.6, 404.31) * mm});
            skLineSegment(sketch, "E458.top", {"start": v(0, 220.11) * mm, "end": v(101.6, 220.11) * mm});
            skLineSegment(sketch, "E458.left", {"start": v(0, 404.31) * mm, "end": v(0, 220.11) * mm});
            skLineSegment(sketch, "E458.right", {"start": v(101.6, 404.31) * mm, "end": v(101.6, 220.11) * mm});
            skSolve(sketch);
        }
        {
            var Q0;
            Q0=makeQuery(id+"F20.imprint","IMPRINT",FACE,{"disambiguationData":[TD([[makeQuery(id+"F20.imprint","IMPRINT",EDGE,{"derivedFrom":sQuery(id+"F20.wireOp",EDGE,"E458.bottom")}),-1.0]])]});
            extrude(context, id + "F21", {"entities" : qUnion([Q0]), "depth" : 19 * mm, "offsetDistance" : 25 * mm});
        }
    });
